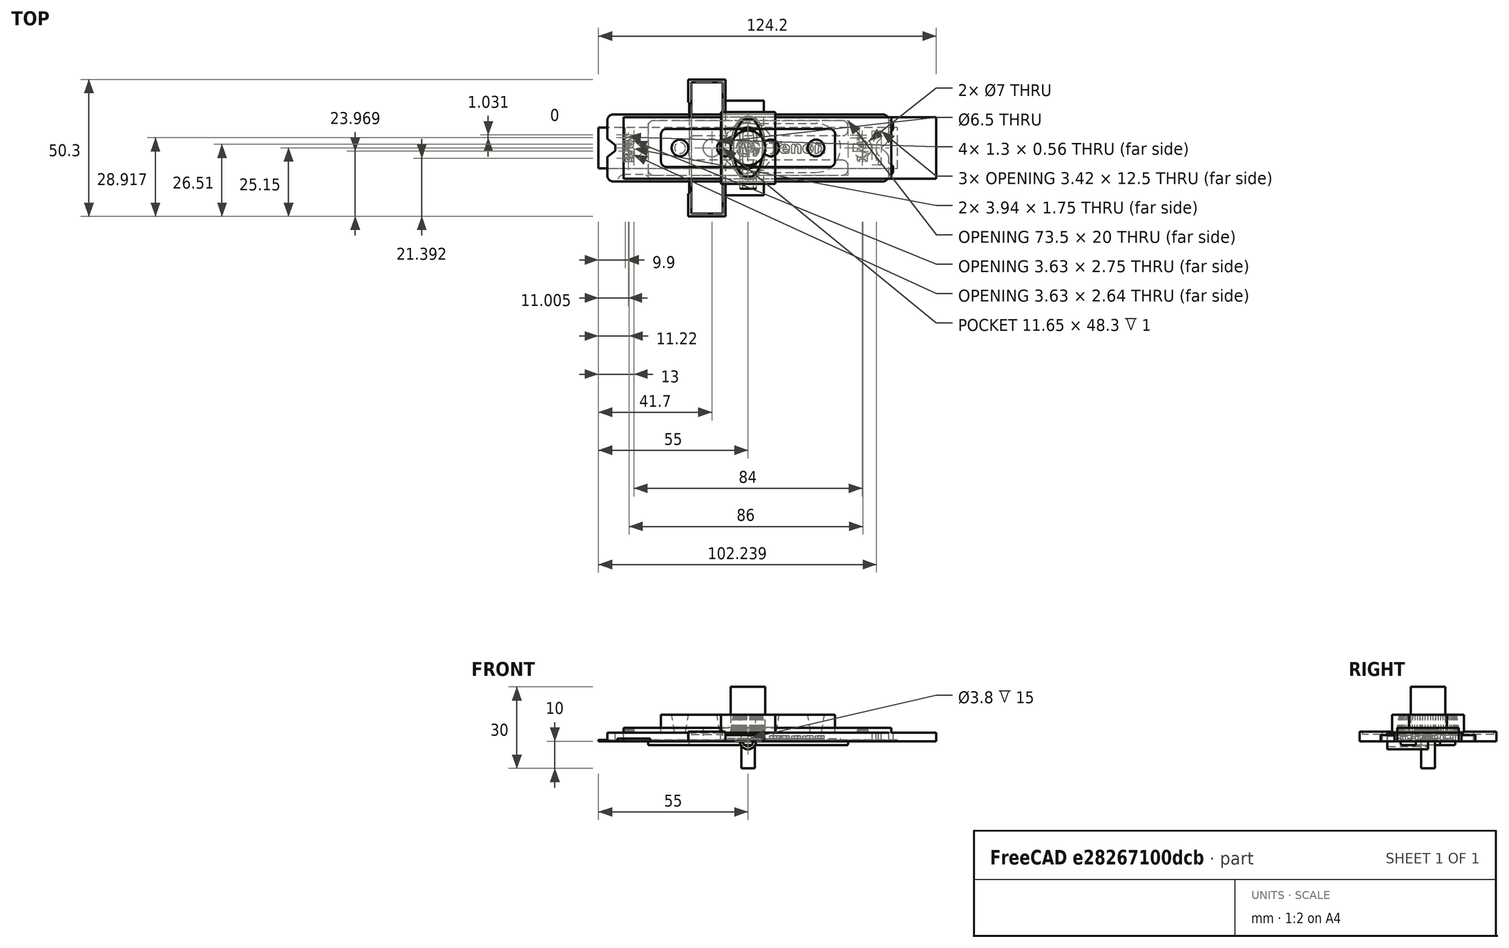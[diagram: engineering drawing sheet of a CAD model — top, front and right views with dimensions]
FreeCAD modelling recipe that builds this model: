
FCSTD DOCUMENT  (FreeCAD 1.1R20260325 (Git shallow))
Label: FMT Guide
License: All rights reserved
LicenseURL: http://en.wikipedia.org/wiki/All_rights_reserved
objects: Sketcher::SketchObject×25, PartDesign::Pad×16, App::Point×10, PartDesign::Body×10, PartDesign::Pocket×5, Part::Part2DObjectPython×4, Part::Extrusion×4, Part::Fuse×3, Part::MultiFuse×3, PartDesign::Plane×2, Part::Cut×2, Mesh::Feature×2, Spreadsheet::Sheet×1, Part::DatumPlane×1, PartDesign::Fillet×1, Part::Scale×1, Part::Loft×1, PartDesign::LinearPattern×1
note: 148 computed .brp shape members not serialized (recipe doc carries the construction recipe); baked Part::Feature solids carry a one-line shape summary decoded from their .brp

FEATURE [Sketcher::SketchObject] Sketch  label="Base Outline"
  ArcFitTolerance = 1e-06
  AttachmentSupport = -> [XY_Plane]
  ExternalTypes = [0]
  FullyConstrained = true
  MakeInternals = false
  MapMode = 5
  _ExternalGeoVersion = 0
  expr: Constraints[12] = Spreadsheet.Base_Corner_Radious
  expr: Constraints[18] = Spreadsheet.Base_Width
  expr: Constraints[19] = Spreadsheet.Base_Length
  sketch-geometry (32):
    g0: LineSegment StartX=-49.55 StartY=-12.32 StartZ=0 EndX=49.55 EndY=-12.32 EndZ=0
    g1: LineSegment [constr] StartX=51.75 StartY=-10.12 StartZ=0 EndX=51.75 EndY=10.12 EndZ=0
    g2: LineSegment StartX=49.55 StartY=12.32 StartZ=0 EndX=-49.55 EndY=12.32 EndZ=0
    g3: ArcOfCircle CenterX=-49.55 CenterY=10.12 CenterZ=0 NormalX=0 NormalY=0 NormalZ=1 AngleXU=0 Radius=2.2 StartAngle=1.5708 EndAngle=3.14159
    g4: ArcOfCircle CenterX=-49.55 CenterY=-10.12 CenterZ=0 NormalX=0 NormalY=0 NormalZ=1 AngleXU=0 Radius=2.2 StartAngle=3.14159 EndAngle=4.71239
    g5: ArcOfCircle CenterX=49.55 CenterY=-10.12 CenterZ=0 NormalX=0 NormalY=0 NormalZ=1 AngleXU=0 Radius=2.2 StartAngle=4.71239 EndAngle=6.28319
    g6: ArcOfCircle CenterX=49.55 CenterY=10.12 CenterZ=0 NormalX=0 NormalY=0 NormalZ=1 AngleXU=0 Radius=2.2 StartAngle=4e-16 EndAngle=1.5708
    g7: GeomPoint [constr] X=51.75 Y=-12.32 Z=0
    g8: LineSegment StartX=51.75 StartY=10.12 StartZ=0 EndX=51.75 EndY=3.625 EndZ=0
    g9: LineSegment StartX=51.75 StartY=-10.12 StartZ=0 EndX=51.75 EndY=-3.625 EndZ=0
    g10: ArcOfCircle CenterX=-49.55 CenterY=3.61127 CenterZ=0 NormalX=0 NormalY=0 NormalZ=1 AngleXU=0 Radius=2.2 StartAngle=3.14159 EndAngle=3.92699
    g11: ArcOfCircle CenterX=-49.55 CenterY=-3.61127 CenterZ=0 NormalX=0 NormalY=0 NormalZ=1 AngleXU=0 Radius=2.2 StartAngle=2.35619 EndAngle=3.14159
    g12: LineSegment StartX=51.5641 StartY=3.23597 StartZ=0 EndX=48.9359 EndY=1.11403 EndZ=0
    g13: LineSegment StartX=48.75 StartY=0.725 StartZ=0 EndX=48.75 EndY=-0.725 EndZ=0
    g14: LineSegment StartX=48.9359 StartY=-1.11403 StartZ=0 EndX=51.5641 EndY=-3.23597 EndZ=0
    g15: ArcOfCircle CenterX=51.25 CenterY=3.625 CenterZ=0 NormalX=0 NormalY=0 NormalZ=1 AngleXU=0 Radius=0.5 StartAngle=5.39161 EndAngle=6.28319
    g16: ArcOfCircle CenterX=51.25 CenterY=-3.625 CenterZ=0 NormalX=0 NormalY=0 NormalZ=1 AngleXU=0 Radius=0.5 StartAngle=6.28319 EndAngle=7.17476
    g17: ArcOfCircle CenterX=49.25 CenterY=-0.725 CenterZ=0 NormalX=0 NormalY=0 NormalZ=1 AngleXU=0 Radius=0.5 StartAngle=3.14159 EndAngle=4.03317
    g18: ArcOfCircle CenterX=49.25 CenterY=0.725 CenterZ=0 NormalX=0 NormalY=0 NormalZ=1 AngleXU=0 Radius=0.5 StartAngle=2.25002 EndAngle=3.14159
    g19: LineSegment StartX=-51.1056 StartY=2.05563 StartZ=0 EndX=-49.05 EndY=0 EndZ=0
    g20: LineSegment StartX=-49.05 StartY=0 StartZ=0 EndX=-51.1056 EndY=-2.05563 EndZ=0
    g21: LineSegment StartX=-48.95 StartY=5.75 StartZ=0 EndX=-48.95 EndY=3.5 EndZ=0
    g22: LineSegment StartX=-47.95 StartY=5.75 StartZ=0 EndX=-47.95 EndY=4.6 EndZ=0
    g23: ArcOfCircle CenterX=-48.45 CenterY=5.75 CenterZ=0 NormalX=0 NormalY=0 NormalZ=1 AngleXU=0 Radius=0.5 StartAngle=1e-16 EndAngle=3.14159
    g24: LineSegment StartX=-48.95 StartY=-3.5 StartZ=0 EndX=-48.95 EndY=-5.75 EndZ=0
    g25: LineSegment StartX=-47.95 StartY=-4.6 StartZ=0 EndX=-47.95 EndY=-5.75 EndZ=0
    g26: ArcOfCircle CenterX=-48.45 CenterY=-5.75 CenterZ=0 NormalX=0 NormalY=0 NormalZ=1 AngleXU=0 Radius=0.5 StartAngle=3.14159 EndAngle=6.28319
    g27: ArcOfCircle CenterX=-51.1056 CenterY=0 CenterZ=0 NormalX=0 NormalY=0 NormalZ=1 AngleXU=0 Radius=4.11057 StartAngle=5.26441 EndAngle=7.30196
    g28: ArcOfCircle CenterX=-51.1056 CenterY=0 CenterZ=0 NormalX=0 NormalY=0 NormalZ=1 AngleXU=0 Radius=5.57835 StartAngle=5.31366 EndAngle=7.25271
    g29: LineSegment StartX=-51.75 StartY=10.12 StartZ=0 EndX=-51.75 EndY=3.61127 EndZ=0
    g30: LineSegment StartX=-51.75 StartY=-3.61127 StartZ=0 EndX=-51.75 EndY=-10.12 EndZ=0
    g31: GeomPoint X=50.25 Y=2.175 Z=0
  constraints (79):
    c: Tangent(g0,g4) = -1.5708
    c: Tangent(g0,g5) = -1.5708
    c: Tangent(g1,g5) = -1.5708
    c: Tangent(g1,g6) = -1.5708
    c: Tangent(g2,g6) = -1.5708
    c: Tangent(g2,g3) = -1.5708
    c: Vertical(g1)
    c: Horizontal(g0)
    c: Horizontal(g2)
    c: Equal(g4,g5)
    c: PointOnObject(g7,g0)
    c: PointOnObject(g7,g1)
    c: Radius(g6) = 2.2
    c: Symmetric(g3,g6,g-2)
    c: Symmetric(g3,g4,g-1)
    c: Tangent(g6,g8)
    c: Coincident(g9,g1)
    c: Coincident(g8,g1)
    c: DistanceY(g0,g2) = 24.64
    c: DistanceX(g3,g1) = 103.5
    c: Equal(g3,g10)
    c: Tangent(g8,g15) = 1.5708
    c: Tangent(g12,g15) = 1.5708
    c: Tangent(g9,g16) = -1.5708
    c: Tangent(g14,g16) = 1.5708
    c: Tangent(g13,g17) = -1.5708
    c: Tangent(g14,g17) = -1.5708
    c: Tangent(g12,g18) = -1.5708
    c: Tangent(g13,g18) = -1.5708
    c: Equal(g15,g18)
    c: Equal(g18,g17)
    c: Equal(g17,g16)
    c: Radius(g15) = 0.5
    c: Symmetric(g18,g17,g-1)
    c: Symmetric(g15,g16,g-1)
    c: DistanceY(g16,g15) = 7.25
    c: DistanceY(g17,g18) = 1.45
    c: DistanceX(g18,g15) = 2
    c: Equal(g5,g6)
    c: PointOnObject(g19,g-1)
    c: Coincident(g20,g19)
    c: Angle(g19,g20) = 1.5708
    c: Tangent(g19,g10) = -1.5708
    c: Tangent(g20,g11) = -1.5708
    c: Symmetric(g10,g11,g-1)
    c: DistanceX(g10,g19) = 2.7
    c: Vertical(g21)
    c: Vertical(g22)
    c: Tangent(g23,g21) = -1.5708
    c: Tangent(g23,g22) = 1.5708
    c: Vertical(g22,g25)
    c: Vertical(g21,g24)
    c: Radius(g23) = 0.5
    c: Vertical(g24)
    c: Vertical(g25)
    c: Coincident(g26,g24)
    c: Coincident(g26,g25)
    c: Equal(g26,g23)
    c: Symmetric(g26,g23,g-1)
    c: Coincident(g27,g21)
    c: Coincident(g24,g27)
    c: PointOnObject(g27,g-1)
    c: Coincident(g28,g22)
    c: Coincident(g28,g25)
    c: Coincident(g27,g28)
    c: DistanceY(g26,g23) = 11.5
    c: DistanceX(g10,g23) = 3.3
    c: DistanceY(g21,g22) = 1.1
    c: DistanceY(g24,g21) = 7
    c: Vertical(g10,g27)
    c: Vertical(g30)
    c: Vertical(g29)
    c: Tangent(g10,g29) = -1.5708
    c: Tangent(g30,g11) = -1.5708
    c: Tangent(g3,g29) = -1.5708
    c: Tangent(g30,g4) = -1.5708
    c: DistanceY(g18,g15) = 2.9
    c: DistanceX(g19,g13) = 97.8
    c: Symmetric(g12,g12,g31)
FEATURE [Spreadsheet::Sheet] Spreadsheet
  cells = A1='Base; A2='Upper Title; B2(Upper_Title)='3/8"; A3='Lower Title; B3(Lower_Title)='1/4"; A4='Base Width; B4(Base_Width)=24.64; C4='Width of base of guide; A5='Base Length; B5(Base_Length)=103.5; C5='Length of base of guide; A6='Base Thickness; B6(Base_Thickness)=3.1; C6='Thickness of base of guide; A7='Base Corner Radious; B7(Base_Corner_Radious)=2.2; C7='Radii of base curves; A9='Lower Plane; B9(Lower_Plane)==Base_Thickness + 0.1; C9='Lower plane of guide portion; A10='Upper Plane; B10(Upper_Plane)==Lower_Plane + 6.5; C10='Upper plane of guide portion; A12='Pin Bottom Width; B12(Pin_Bottom_Width)=4; C12='Diameter of narrow point of Pin; A13='Pin Top Width; B13(Pin_Top_Width)=5; C13='Diameter of wide point of pin; A14='Pin Angle; B14(Pin_Angle)=9.22; A15='Calculated Pin Angle; B15==atan((Pin_Top_Width - Pin_Bottom_Width) / 3) / 2; A16='Bump Thickness; B16(Bump_Thickness)==Base_Thickness - 0.5; A17='Bump Width; B17(Bump_Width)=3.2; A18='Bump Spacing; B18(Bump_Spacing)=15.7; A19='Margin; B19(Margin)=1; A20='Pin Spacing; B20(Pin_Spacing)=250; A22='Mortise & Tenon; A23='Movement Ratio; B23(Movement_Ratio)=2; C23='Y-scale for guide; A24='Width; B24(Width)=6.35; C24='Width of tenon/mortise; A25='Length; B25(Length)=9.525; C25='Length of tenon/mortise; A26='Router Diameter; B26(Router_Diameter)==Width; C26='Always equals width of tenon; A27='Fix; B27(Fix)=0; C27='Hack for -ve dimension; A28='Width Delta; B28(Width_Delta)=1.75; C28='Extra Tenon Width; A29='Length Delta; B29(Length_Delta)=1; C29='Extra Tenon Length; A30='Slot Delta; B30(Slot_Delta)=1.35; C30='Extra Mortise Length; A32='Dowel Centres; A33='Dowel Extent; B33(Dowel_Extent)=50; C33='Extent of Dowels; A34='Dowel Length; B34(Dowel_Length)==Dowel_Extent + 10; C34='Length of base (calculated); A35='Dowel Width; B35(Dowel_Width)=10; C35='Width of base; A36='Dowel Number; B36(Dowel_Number)=4; A38='Centering Disk; A39='Centering Title; B39(Centering_Title)='1/2"; A40='Centering Disk Diameter; B40(Centering_Disk_Diameter)=18.8; A41='Centering Disk Thickness; B41(Centering_Disk_Thickness)=5; A42='Centering Post Diameter; B42(Centering_Post_Diameter)=12.7; A43='Centering Post Length; B43(Centering_Post_Length)=10; A45='Y Tenon; A46='Tenon Base Width; B46(Tenon_Base_Width)=20; A47='Tenon Extra Length; B47(Tenon_Extra_Length)=20
FEATURE [PartDesign::Plane] DatumPlane  label="Upper Plane"
  AttachmentOffset = pos=(0,0,9.7) rot=(0,0,1;0rad)
  AttachmentSupport = -> [XY_Plane]
  Length = 160.151
  MapMode = 5
  Placement = pos=(0,0,9.7) rot=(0,0,1;0rad)
  ResizeMode = 0
  Width = 133.592
  expr: .AttachmentOffset.Base.z = Spreadsheet.Upper_Plane
FEATURE [PartDesign::Plane] DatumPlane001  label="Mid Plane"
  AttachmentOffset = pos=(0,0,3.2) rot=(0,0,1;0rad)
  AttachmentSupport = -> [XY_Plane]
  Length = 160.151
  MapMode = 5
  Placement = pos=(0,0,3.2) rot=(0,0,1;0rad)
  ResizeMode = 0
  Width = 133.592
  expr: .AttachmentOffset.Base.z = Spreadsheet.Lower_Plane
FEATURE [Part::DatumPlane] DatumPlane002  label="Base Surface Plane"
  AttachmentSupport = -> [Origin]
  Placement = pos=(0,0,3.1) rot=(0,0,1;0rad)
  expr: .Placement.Base.z = Spreadsheet.Base_Thickness
FEATURE [PartDesign::Pad] Pad  label="Base Base"
  Direction = (0,0,1)
  Length = 3.1
  Length2 = 10
  Profile = -> Sketch
  ReferenceAxis = -> Sketch [N_Axis]
  SideType = 0
  Suppressed = false
  Type = 0
  Type2 = 0
  expr: Length = Spreadsheet.Base_Thickness
FEATURE [Part::Part2DObjectPython] ShapeString001  label="Label"  # Draft 2D object (typed FeaturePython)
  FontFile = <path>
  Fuse = false
  Justification = 4
  JustificationReference = 0
  KeepLeftMargin = false
  MakeFace = true
  ObliqueAngle = 0
  Placement = pos=(44,0,3.1) rot=(0,0,1;4.71239rad)
  ScaleToSize = true
  Size = 3.5
  String = 3/8"
  Tracking = 0
  expr: .Placement.Base.z = Spreadsheet.Base_Thickness
  expr: String = Spreadsheet.Upper_Title
FEATURE [Part::Extrusion] Extrude  label="Extrude Upper"
  Base = -> ShapeString001
  Dir = (0,0,1)
  DirMode = 2
  FaceMakerClass = Part::FaceMakerBullseye
  FaceMakerMode = 3
  InnerWireTaper = 0
  LengthFwd = 1
  LengthRev = 0
  Solid = false
  Symmetric = false
FEATURE [App::Point] Origin007  label="Origin008"
  Role = Origin
FEATURE [Sketcher::SketchObject] Sketch008
  ArcFitTolerance = 1e-06
  AttachmentSupport = -> [Origin006]
  ExternalTypes = [0]
  FullyConstrained = true
  MakeInternals = false
  MapMode = 5
  _ExternalGeoVersion = 1
  expr: Constraints[1] = Spreadsheet.Centering_Disk_Diameter
  sketch-geometry (1):
    g0: Circle CenterX=0 CenterY=0 CenterZ=0 NormalX=0 NormalY=0 NormalZ=1 AngleXU=0 Radius=9.4
  constraints (2):
    c: Coincident(g0,g-1)
    c: Diameter(g0) = 18.8
FEATURE [PartDesign::Pad] Pad002  label="Base001"
  Direction = (0,0,1)
  Length = 5
  Length2 = 10
  Profile = -> Sketch008
  ReferenceAxis = -> Sketch008 [N_Axis]
  SideType = 0
  Suppressed = false
  Type = 0
  Type2 = 0
  expr: Length = Spreadsheet.Centering_Disk_Thickness
FEATURE [Sketcher::SketchObject] Sketch009
  ArcFitTolerance = 1e-06
  AttachmentSupport = -> [Pad002]
  ExternalTypes = [0]
  FullyConstrained = true
  MakeInternals = false
  MapMode = 5
  Placement = pos=(0,0,5) rot=(0,0,1;0rad)
  _ExternalGeoVersion = 1
  expr: Constraints[1] = Spreadsheet.Centering_Post_Diameter
  sketch-geometry (1):
    g0: Circle CenterX=0 CenterY=0 CenterZ=0 NormalX=0 NormalY=0 NormalZ=1 AngleXU=0 Radius=6.35
  constraints (2):
    c: Coincident(g0,g-1)
    c: Diameter(g0) = 12.7
FEATURE [PartDesign::Pad] Pad003  label="Arbor"
  BaseFeature = -> Pad002
  Direction = (0,0,1)
  Length = 15
  Length2 = 10
  Profile = -> Sketch009
  ReferenceAxis = -> Sketch009 [N_Axis]
  SideType = 0
  Suppressed = false
  Type = 0
  Type2 = 0
  expr: Length = Spreadsheet.Centering_Post_Length + Spreadsheet.Centering_Disk_Thickness
FEATURE [PartDesign::Body] Body003  label="Centering Bare"
  AllowCompound = false
  Group = -> [Sketch008,Pad002,Sketch009,Pad003]
  Origin = -> Origin006
  Tip = -> Pad003
FEATURE [Sketcher::SketchObject] Sketch013  label="Outline"
  ArcFitTolerance = 1e-06
  AttachmentSupport = -> [DatumPlane002]
  ExternalTypes = [0]
  FullyConstrained = true
  MakeInternals = false
  MapMode = 5
  Placement = pos=(0,0,3.1) rot=(0,0,1;0rad)
  _ExternalGeoVersion = 1
  expr: Constraints[18] = Spreadsheet.Dowel_Length
  expr: Constraints[19] = Spreadsheet.Dowel_Width
  sketch-geometry (10):
    g0: LineSegment StartX=-32 StartY=5 StartZ=0 EndX=-32 EndY=-5 EndZ=0
    g1: LineSegment StartX=-30 StartY=-7 StartZ=0 EndX=30 EndY=-7 EndZ=0
    g2: LineSegment StartX=32 StartY=-5 StartZ=0 EndX=32 EndY=5 EndZ=0
    g3: LineSegment StartX=30 StartY=7 StartZ=0 EndX=-30 EndY=7 EndZ=0
    g4: ArcOfCircle CenterX=-30 CenterY=5 CenterZ=0 NormalX=0 NormalY=0 NormalZ=1 AngleXU=0 Radius=2 StartAngle=1.5708 EndAngle=3.14159
    g5: ArcOfCircle CenterX=-30 CenterY=-5 CenterZ=0 NormalX=0 NormalY=0 NormalZ=1 AngleXU=0 Radius=2 StartAngle=3.14159 EndAngle=4.71239
    g6: ArcOfCircle CenterX=30 CenterY=-5 CenterZ=0 NormalX=0 NormalY=0 NormalZ=1 AngleXU=0 Radius=2 StartAngle=4.71239 EndAngle=6.28319
    g7: ArcOfCircle CenterX=30 CenterY=5 CenterZ=0 NormalX=0 NormalY=0 NormalZ=1 AngleXU=0 Radius=2 StartAngle=0 EndAngle=1.5708
    g8: GeomPoint [constr] X=-32 Y=7 Z=0
    g9: GeomPoint [constr] X=32 Y=-7 Z=0
  constraints (22):
    c: Tangent(g0,g4) = -1.5708
    c: Tangent(g0,g5) = -1.5708
    c: Tangent(g1,g5) = -1.5708
    c: Tangent(g1,g6) = -1.5708
    c: Tangent(g2,g6) = -1.5708
    c: Tangent(g2,g7) = -1.5708
    c: Tangent(g3,g7) = -1.5708
    c: Tangent(g3,g4) = -1.5708
    c: Vertical(g0)
    c: Vertical(g2)
    c: Horizontal(g1)
    c: Horizontal(g3)
    c: Equal(g4,g5)
    c: PointOnObject(g8,g0)
    c: PointOnObject(g8,g3)
    c: PointOnObject(g9,g1)
    c: PointOnObject(g9,g2)
    c: Radius(g7) = 2
    c: DistanceX(g4,g7) = 60
    c: DistanceY(g6,g7) = 10
    c: Symmetric(g7,g6,g-1)
    c: Symmetric(g4,g7,g-2)
FEATURE [PartDesign::Pad] Pad004  label="Dowel Base"
  Direction = (0,0,1)
  Length = 6.6
  Length2 = 10
  Placement = pos=(0,0,3.1) rot=(0,0,1;0rad)
  Profile = -> Sketch013
  ReferenceAxis = -> Sketch013 [N_Axis]
  SideType = 0
  Suppressed = false
  Type = 0
  Type2 = 0
  expr: Length = Spreadsheet.Upper_Plane - Spreadsheet.Base_Thickness
FEATURE [App::Point] Origin009  label="Origin011"
  Role = Origin
FEATURE [App::Point] Origin002  label="Origin"
  Role = Origin
FEATURE [Part::Part2DObjectPython] ShapeString  # Draft 2D object (typed FeaturePython)
  FontFile = <path>
  Fuse = false
  Justification = 4
  JustificationReference = 0
  KeepLeftMargin = false
  MakeFace = true
  ObliqueAngle = 0
  Placement = pos=(0,0,0) rot=(1,0,0;3.14159rad)
  ScaleToSize = false
  Size = 3
  String = 1/2"
  Tracking = 0
  expr: String = Spreadsheet.Centering_Title
FEATURE [Part::Extrusion] Extrude001  label="Description"
  Base = -> ShapeString
  Dir = (0,0,-1)
  DirMode = 2
  FaceMakerClass = Part::FaceMakerBullseye
  FaceMakerMode = 3
  InnerWireTaper = 0
  LengthFwd = 1
  LengthRev = 0
  Reversed = true
  Solid = false
  Symmetric = false
FEATURE [Part::Part2DObjectPython] ShapeString002  # Draft 2D object (typed FeaturePython)
  FontFile = <path>
  Fuse = false
  Justification = 4
  JustificationReference = 0
  KeepLeftMargin = false
  MakeFace = true
  ObliqueAngle = 0
  Placement = pos=(-42,0,3.1) rot=(0,0,1;4.71239rad)
  ScaleToSize = true
  Size = 3.5
  String = 1/4"
  Tracking = 0
  expr: .Placement.Base.z = Spreadsheet.Base_Thickness
  expr: String = Spreadsheet.Lower_Title
FEATURE [Part::Extrusion] Extrude002  label="Extrude Lower"
  Base = -> ShapeString002
  Dir = (0,0,1)
  DirMode = 2
  FaceMakerClass = Part::FaceMakerBullseye
  FaceMakerMode = 3
  InnerWireTaper = 0
  LengthFwd = 1
  LengthRev = 0
  Solid = false
  Symmetric = false
FEATURE [Part::Fuse] Fusion006  label="UpperLowerLabel"
  Base = -> Extrude
  Tool = -> Extrude002
FEATURE [Part::Cut] Cut002  label="Centering"
  Base = -> Body003
  Tool = -> Extrude001
FEATURE [App::Point] Origin011  label="Origin013"
  Role = Origin
FEATURE [Sketcher::SketchObject] Sketch014  label="Tenon Surround Outline"
  ArcFitTolerance = 1e-06
  AttachmentSupport = -> [DatumPlane002]
  ExternalTypes = [0]
  FullyConstrained = true
  MakeInternals = false
  MapMode = 5
  Placement = pos=(0,0,3.1) rot=(0,0,1;0rad)
  _ExternalGeoVersion = 1
  expr: Constraints[10] = (Spreadsheet.Length - Spreadsheet.Width) * 2 + Spreadsheet.Tenon_Extra_Length
  expr: Constraints[11] = Spreadsheet.Tenon_Base_Width
  sketch-geometry (5):
    g0: LineSegment StartX=-10 StartY=13.175 StartZ=0 EndX=-10 EndY=-13.175 EndZ=0
    g1: LineSegment StartX=-10 StartY=-13.175 StartZ=0 EndX=10 EndY=-13.175 EndZ=0
    g2: LineSegment StartX=10 StartY=-13.175 StartZ=0 EndX=10 EndY=13.175 EndZ=0
    g3: LineSegment StartX=10 StartY=13.175 StartZ=0 EndX=-10 EndY=13.175 EndZ=0
    g4: GeomPoint [constr] X=0 Y=0 Z=0
  constraints (12):
    c: Coincident(g0,g1)
    c: Coincident(g1,g2)
    c: Coincident(g2,g3)
    c: Coincident(g3,g0)
    c: Vertical(g0)
    c: Vertical(g2)
    c: Horizontal(g1)
    c: Horizontal(g3)
    c: Symmetric(g2,g0,g4)
    c: Coincident(g4,g-1)
    c: DistanceY(g2,g2) = 26.35
    c: Distance(g3,g3) = 20
FEATURE [PartDesign::Pad] Pad005  label="X Tenon Surround"
  Direction = (0,0,1)
  Length = 6.6
  Length2 = 10
  Placement = pos=(0,0,3.1) rot=(0,0,1;0rad)
  Profile = -> Sketch014
  ReferenceAxis = -> Sketch014 [N_Axis]
  SideType = 0
  Suppressed = false
  Type = 0
  Type2 = 0
  expr: Length = Spreadsheet.Upper_Plane - Spreadsheet.Base_Thickness
FEATURE [Sketcher::SketchObject] Sketch016  label="Y Tenon Outline"
  ArcFitTolerance = 1e-06
  AttachmentSupport = -> [DatumPlane002]
  ExternalTypes = [0]
  FullyConstrained = true
  MakeInternals = false
  MapMode = 5
  Placement = pos=(0,0,3.1) rot=(0,0,1;0rad)
  _ExternalGeoVersion = 1
  expr: Constraints[0] = Spreadsheet.Pin_Bottom_Width / 2
  expr: Constraints[24] = Spreadsheet.Length - Spreadsheet.Router_Diameter + Spreadsheet.Slot_Delta
  expr: Constraints[25] = Spreadsheet.Pin_Spacing / 2
  expr: Constraints[7] = Spreadsheet.Router_Diameter
  sketch-geometry (24):
    g0: ArcOfCircle CenterX=0.0204773 CenterY=4.525 CenterZ=0 NormalX=0 NormalY=0 NormalZ=1 AngleXU=0 Radius=2 StartAngle=6.27413 EndAngle=9.41573
    g1: ArcOfCircle CenterX=0.0204773 CenterY=-4.525 CenterZ=0 NormalX=0 NormalY=0 NormalZ=1 AngleXU=0 Radius=2 StartAngle=3.15064 EndAngle=6.29224
    g2: GeomPoint [constr] X=125 Y=0 Z=0
    g3: ArcOfCircle [constr] CenterX=125 CenterY=2.2625 CenterZ=0 NormalX=0 NormalY=0 NormalZ=1 AngleXU=0 Radius=3.175 StartAngle=1e-16 EndAngle=3.14159
    g4: ArcOfCircle [constr] CenterX=125 CenterY=-2.2625 CenterZ=0 NormalX=0 NormalY=0 NormalZ=1 AngleXU=0 Radius=3.175 StartAngle=3.14159 EndAngle=6.28319
    g5: LineSegment [constr] StartX=128.175 StartY=2.2625 StartZ=0 EndX=128.175 EndY=-2.2625 EndZ=0
    g6: LineSegment [constr] StartX=121.825 StartY=2.2625 StartZ=0 EndX=121.825 EndY=-2.2625 EndZ=0
    g7: Circle [constr] CenterX=125 CenterY=2.2625 CenterZ=0 NormalX=0 NormalY=0 NormalZ=1 AngleXU=0 Radius=3.175
    g8: GeomPoint [constr] X=249.98 Y=0 Z=0
    g9: LineSegment [constr] StartX=0.0204773 StartY=4.525 StartZ=0 EndX=125 EndY=2.2625 EndZ=0
    g10: LineSegment [constr] StartX=125 StartY=2.2625 StartZ=0 EndX=249.98 EndY=0 EndZ=0
    g11: LineSegment [constr] StartX=0 StartY=0 StartZ=0 EndX=125 EndY=0 EndZ=0
    g12: LineSegment [constr] StartX=125 StartY=0 StartZ=0 EndX=250 EndY=0 EndZ=0
    g13: LineSegment [constr] StartX=-1.97944 StartY=4.5431 StartZ=0 EndX=2.0204 EndY=4.5069 EndZ=0
    g14: LineSegment [constr] StartX=-1.97944 StartY=-4.5431 StartZ=0 EndX=2.0204 EndY=-4.5069 EndZ=0
    g15: Circle [constr] CenterX=0 CenterY=0 CenterZ=0 NormalX=0 NormalY=0 NormalZ=1 AngleXU=0 Radius=2
    g16: ArcOfCircle CenterX=499.969 CenterY=4.93e-14 CenterZ=0 NormalX=0 NormalY=0 NormalZ=1 AngleXU=0 Radius=497.969 StartAngle=3.13254 EndAngle=3.15064
    g17: GeomPoint [constr] X=2 Y=0 Z=0
    g18: ArcOfCircle CenterX=499.969 CenterY=-6.03e-14 CenterZ=0 NormalX=0 NormalY=0 NormalZ=1 AngleXU=0 Radius=501.969 StartAngle=3.13254 EndAngle=3.15064
    g19: GeomPoint [constr] X=-2 Y=0 Z=0
    g20: GeomPoint [constr] X=125 Y=5.4375 Z=0
    g21: GeomPoint [constr] X=125 Y=-5.4375 Z=0
    g22: GeomPoint [constr] X=0 Y=6.5249 Z=0
    g23: GeomPoint [constr] X=0 Y=-6.5249 Z=0
  constraints (58):
    c: Radius(g0) = 2
    c: PointOnObject(g2,g-1)
    c: Tangent(g3,g5) = 1.5708
    c: Tangent(g3,g6) = -1.5708
    c: Tangent(g4,g5) = 1.5708
    c: Tangent(g4,g6) = -1.5708
    c: Equal(g3,g4)
    c: Diameter(g3) = 6.35
    c: Symmetric(g3,g4,g-1)
    c: Vertical(g3,g2)
    c: Equal(g7,g3)
    c: DistanceY(g1,g0) = 9.05
    c: PointOnObject(g8,g-1)
    c: Coincident(g9,g0)
    c: Coincident(g9,g7)
    c: Coincident(g10,g7)
    c: Coincident(g10,g8)
    c: Parallel(g10,g9)
    c: Coincident(g11,g2)
    c: Coincident(g12,g2)
    c: PointOnObject(g12,g-1)
    c: Equal(g12,g11)
    c: Equal(g11,g10)
    c: Equal(g10,g9)
    c: Distance(g3,g4) = 4.525
    c: Distance(g11) = 125
    c: Coincident(g11,g-1)
    c: Symmetric(g0,g1,g-1)
    c: Coincident(g13,g0)
    c: Coincident(g13,g0)
    c: PointOnObject(g0,g13)
    c: Symmetric(g0,g1,g-1)
    c: Coincident(g14,g1)
    c: Coincident(g14,g1)
    c: PointOnObject(g1,g14)
    c: Coincident(g15,g11)
    c: Equal(g15,g1)
    c: Coincident(g16,g1)
    c: Tangent(g16,g15)
    c: PointOnObject(g17,g16)
    c: PointOnObject(g17,g-1)
    c: Tangent(g16,g0) = 1.5708
    c: Coincident(g18,g0)
    c: Coincident(g18,g1)
    c: PointOnObject(g19,g18)
    c: PointOnObject(g19,g-1)
    c: Tangent(g18,g15)
    c: PointOnObject(g20,g3)
    c: PointOnObject(g21,g4)
    c: Vertical(g21,g4)
    c: Vertical(g4,g20)
    c: DistanceY(g21,g20) = 10.875
    c: Coincident(g7,g3)
    c: PointOnObject(g22,g0)
    c: PointOnObject(g23,g1)
    c: PointOnObject(g23,g-2)
    c: PointOnObject(g22,g-2)
    c: Distance(g22,g23) = 13.0498
FEATURE [Sketcher::SketchObject] Sketch019  label="Reinforcing Outline"
  ArcFitTolerance = 1e-06
  ExternalTypes = [0]
  FullyConstrained = true
  MakeInternals = false
  MapMode = 5
  Placement = pos=(0,0,0) rot=(1,0,0;3.14159rad)
  _ExternalGeoVersion = 1
  expr: Constraints[9] = Spreadsheet.Base_Length - 2 * 15
  sketch-geometry (24):
    g0: LineSegment StartX=-34.75 StartY=10 StartZ=0 EndX=34.75 EndY=10 EndZ=0
    g1: LineSegment StartX=36.75 StartY=8 StartZ=0 EndX=36.75 EndY=-8 EndZ=0
    g2: LineSegment StartX=34.75 StartY=-10 StartZ=0 EndX=-34.75 EndY=-10 EndZ=0
    g3: LineSegment StartX=-36.75 StartY=-8 StartZ=0 EndX=-36.75 EndY=-6.5 EndZ=0
    g4: LineSegment StartX=-34.75 StartY=-4.5 StartZ=0 EndX=19.75 EndY=-4.5 EndZ=0
    g5: LineSegment StartX=21.75 StartY=-2.5 StartZ=0 EndX=21.75 EndY=2.5 EndZ=0
    g6: LineSegment StartX=19.75 StartY=4.5 StartZ=0 EndX=-34.75 EndY=4.5 EndZ=0
    g7: LineSegment StartX=-36.75 StartY=6.5 StartZ=0 EndX=-36.75 EndY=8 EndZ=0
    g8: ArcOfCircle CenterX=34.75 CenterY=8 CenterZ=0 NormalX=0 NormalY=0 NormalZ=1 AngleXU=0 Radius=2 StartAngle=0 EndAngle=1.5708
    g9: GeomPoint [constr] X=36.75 Y=10 Z=0
    g10: ArcOfCircle CenterX=34.75 CenterY=-8 CenterZ=0 NormalX=0 NormalY=0 NormalZ=1 AngleXU=0 Radius=2 StartAngle=4.71239 EndAngle=6.28319
    g11: GeomPoint [constr] X=36.75 Y=-10 Z=0
    g12: ArcOfCircle CenterX=-34.75 CenterY=8 CenterZ=0 NormalX=0 NormalY=0 NormalZ=1 AngleXU=0 Radius=2 StartAngle=1.5708 EndAngle=3.14159
    g13: GeomPoint [constr] X=-36.75 Y=10 Z=0
    g14: ArcOfCircle CenterX=-34.75 CenterY=6.5 CenterZ=0 NormalX=0 NormalY=0 NormalZ=1 AngleXU=0 Radius=2 StartAngle=3.14159 EndAngle=4.71239
    g15: GeomPoint [constr] X=-36.75 Y=4.5 Z=0
    g16: ArcOfCircle CenterX=-34.75 CenterY=-6.5 CenterZ=0 NormalX=0 NormalY=0 NormalZ=1 AngleXU=0 Radius=2 StartAngle=1.5708 EndAngle=3.14159
    g17: GeomPoint [constr] X=-36.75 Y=-4.5 Z=0
    g18: ArcOfCircle CenterX=-34.75 CenterY=-8 CenterZ=0 NormalX=0 NormalY=0 NormalZ=1 AngleXU=0 Radius=2 StartAngle=3.14159 EndAngle=4.71239
    g19: GeomPoint [constr] X=-36.75 Y=-10 Z=0
    g20: ArcOfCircle CenterX=19.75 CenterY=2.5 CenterZ=0 NormalX=0 NormalY=0 NormalZ=1 AngleXU=0 Radius=2 StartAngle=2e-16 EndAngle=1.5708
    g21: GeomPoint [constr] X=21.75 Y=4.5 Z=0
    g22: ArcOfCircle CenterX=19.75 CenterY=-2.5 CenterZ=0 NormalX=0 NormalY=0 NormalZ=1 AngleXU=0 Radius=2 StartAngle=4.71239 EndAngle=6.28319
    g23: GeomPoint [constr] X=21.75 Y=-4.5 Z=0
  constraints (51):
    c: Horizontal(g4)
    c: Symmetric(g21,g23,g-1)
    c: Symmetric(g9,g11,g-1)
    c: Symmetric(g15,g17,g-1)
    c: Symmetric(g13,g19,g-1)
    c: Vertical(g7)
    c: Distance(g9,g11) = 20
    c: Distance(g23,g21) = 9
    c: Symmetric(g11,g19,g-2)
    c: DistanceX(g19,g11) = 73.5
    c: DistanceX(g23,g11) = 15
    c: PointOnObject(g9,g0)
    c: PointOnObject(g9,g1)
    c: Tangent(g0,g8) = 1.5708
    c: Tangent(g1,g8) = 1.5708
    c: PointOnObject(g11,g1)
    c: PointOnObject(g11,g2)
    c: Tangent(g1,g10) = 1.5708
    c: Tangent(g2,g10) = 1.5708
    c: PointOnObject(g13,g0)
    c: PointOnObject(g13,g7)
    c: Tangent(g0,g12) = 1.5708
    c: Tangent(g7,g12) = 1.5708
    c: PointOnObject(g15,g6)
    c: PointOnObject(g15,g7)
    c: Tangent(g6,g14) = 1.5708
    c: Tangent(g7,g14) = 1.5708
    c: PointOnObject(g17,g3)
    c: PointOnObject(g17,g4)
    c: Tangent(g3,g16) = 1.5708
    c: Tangent(g4,g16) = 1.5708
    c: PointOnObject(g19,g2)
    c: PointOnObject(g19,g3)
    c: Tangent(g2,g18) = 1.5708
    c: Tangent(g3,g18) = 1.5708
    c: PointOnObject(g21,g5)
    c: PointOnObject(g21,g6)
    c: Tangent(g5,g20) = -1.5708
    c: Tangent(g6,g20) = -1.5708
    c: PointOnObject(g23,g4)
    c: PointOnObject(g23,g5)
    c: Tangent(g4,g22) = -1.5708
    c: Tangent(g5,g22) = -1.5708
    c: Equal(g8,g12)
    c: Equal(g12,g14)
    c: Equal(g14,g16)
    c: Equal(g16,g18)
    c: Equal(g18,g20)
    c: Equal(g20,g22)
    c: Equal(g22,g10)
    c: Radius(g10) = 2
FEATURE [PartDesign::Pad] Pad007  label="Reinforcing"
  BaseFeature = -> Pad
  Direction = (0,-1e-16,-1)
  Length = 1.5
  Length2 = 10
  Profile = -> Sketch019
  ReferenceAxis = -> Sketch019 [N_Axis]
  SideType = 0
  Suppressed = false
  Type = 0
  Type2 = 0
FEATURE [PartDesign::Fillet] Fillet002  label="Reinforcing Fillet"
  Base = -> Pad007 [Face48]
  BaseFeature = -> Pad007
  Radius = 0.5
  SupportTransform = false
  Suppressed = false
  UseAllEdges = false
FEATURE [Sketcher::SketchObject] Sketch020
  ArcFitTolerance = 1e-06
  AttachmentSupport = -> [Fillet002]
  ExternalTypes = [0]
  FullyConstrained = true
  MakeInternals = false
  MapMode = 5
  Placement = pos=(0,0,0) rot=(1,0,0;3.14159rad)
  _ExternalGeoVersion = 1
  expr: Constraints[7] = -Spreadsheet.Base_Width / 2
  sketch-geometry (4):
    g0: ArcOfCircle CenterX=38.5 CenterY=-12.32 CenterZ=0 NormalX=0 NormalY=0 NormalZ=1 AngleXU=0 Radius=2.5 StartAngle=1.5708 EndAngle=4.71239
    g1: ArcOfCircle CenterX=45.5 CenterY=-12.32 CenterZ=0 NormalX=0 NormalY=0 NormalZ=1 AngleXU=0 Radius=2.5 StartAngle=4.71239 EndAngle=7.85398
    g2: LineSegment StartX=38.5 StartY=-9.82 StartZ=0 EndX=45.5 EndY=-9.82 EndZ=0
    g3: LineSegment StartX=38.5 StartY=-14.82 StartZ=0 EndX=45.5 EndY=-14.82 EndZ=0
  constraints (10):
    c: Tangent(g0,g2) = 1.5708
    c: Tangent(g0,g3) = -1.5708
    c: Tangent(g1,g2) = 1.5708
    c: Tangent(g1,g3) = -1.5708
    c: Equal(g0,g1)
    c: Horizontal(g2)
    c: Radius(g1) = 2.5
    c: DistanceY(g0) = -12.32
    c: DistanceX(g0,g1) = 7
    c: DistanceX(g0) = 38.5
FEATURE [PartDesign::Pocket] Pocket  label="Recess"
  BaseFeature = -> Fillet002
  Direction = (0,0,1)
  Length = 1
  Length2 = 5
  Profile = -> Sketch020
  ReferenceAxis = -> Sketch020 [N_Axis]
  SideType = 0
  Suppressed = false
  Type = 0
  Type2 = 0
FEATURE [Sketcher::SketchObject] Sketch005  label="Slot Outline"
  ArcFitTolerance = 1e-06
  AttacherType = Attacher::AttachEngine3D
  ExternalTypes = [0]
  FullyConstrained = false
  MakeInternals = false
  MapMode = 5
  Placement = pos=(0,0,3.1) rot=(0,0,1;0rad)
  _ExternalGeoVersion = 1
  expr: .Placement.Base.z = Spreadsheet.Base_Thickness
  expr: Constraints[24] = Spreadsheet.Length - Spreadsheet.Router_Diameter + Spreadsheet.Pin_Top_Width
  expr: Constraints[7] = Spreadsheet.Length - Spreadsheet.Router_Diameter + Spreadsheet.Slot_Delta
  expr: Constraints[8] = Spreadsheet.Pin_Bottom_Width / 2
  sketch-geometry (11):
    g0: ArcOfCircle CenterX=-2.2625 CenterY=0 CenterZ=0 NormalX=0 NormalY=0 NormalZ=1 AngleXU=0 Radius=2 StartAngle=1.5708 EndAngle=4.71239
    g1: ArcOfCircle CenterX=2.2625 CenterY=0 CenterZ=0 NormalX=0 NormalY=0 NormalZ=1 AngleXU=0 Radius=2 StartAngle=4.71239 EndAngle=7.85398
    g2: LineSegment StartX=-2.2625 StartY=2 StartZ=0 EndX=2.2625 EndY=2 EndZ=0
    g3: LineSegment StartX=-2.2625 StartY=-2 StartZ=0 EndX=2.2625 EndY=-2 EndZ=0
    g4: GeomPoint X=-4.2625 Y=0 Z=0
    g5: GeomPoint X=4.2625 Y=0 Z=0
    g6: LineSegment [constr] StartX=-4.0875 StartY=29.5438 StartZ=0 EndX=-4.0875 EndY=17.568 EndZ=0
    g7: LineSegment [constr] StartX=-4.0875 StartY=17.568 StartZ=0 EndX=4.0875 EndY=17.568 EndZ=0
    g8: LineSegment [constr] StartX=4.0875 StartY=17.568 StartZ=0 EndX=4.0875 EndY=29.5438 EndZ=0
    g9: LineSegment [constr] StartX=4.0875 StartY=29.5438 StartZ=0 EndX=-4.0875 EndY=29.5438 EndZ=0
    g10: GeomPoint [constr] X=0 Y=23.5559 Z=0
  constraints (25):
    c: Tangent(g0,g2) = 1.5708
    c: Tangent(g0,g3) = -1.5708
    c: Tangent(g1,g2) = 1.5708
    c: Tangent(g1,g3) = -1.5708
    c: Equal(g0,g1)
    c: PointOnObject(g0,g-1)
    c: Symmetric(g0,g1,g-2)
    c: Distance(g1,g0) = 4.525
    c: Radius(g1) = 2
    c: PointOnObject(g4,g0)
    c: PointOnObject(g5,g1)
    c: PointOnObject(g4,g-1)
    c: PointOnObject(g5,g-1)
    c: DistanceX(g4,g5) = 8.525
    c: Coincident(g6,g7)
    c: Coincident(g7,g8)
    c: Coincident(g8,g9)
    c: Coincident(g9,g6)
    c: Vertical(g6)
    c: Vertical(g8)
    c: Horizontal(g7)
    c: Horizontal(g9)
    c: Symmetric(g8,g6,g10)
    c: PointOnObject(g10,g-2)
    c: DistanceX(g9,g9) = 8.175
FEATURE [Part::Scale] Scale  label="Scaled Slot Outline"
  Base = -> Sketch005
  Placement = pos=(0,0,9.7) rot=(0,0,1;0rad)
  Uniform = false
  UniformScale = 1
  XScale = 1
  YScale = 1.5
  ZScale = 1
  expr: .Placement.Base.z = Spreadsheet.Upper_Plane
  expr: YScale = 6 / 4
FEATURE [Part::Loft] Loft  label="Slot (Loft)"
  Closed = false
  MaxDegree = 5
  Ruled = false
  Sections = -> [Sketch005,Scale]
  Solid = true
FEATURE [App::Point] Origin013  label="Origin016"
  Role = Origin
FEATURE [Sketcher::SketchObject] Sketch021
  ArcFitTolerance = 1e-06
  AttachmentSupport = -> [Origin012]
  ExternalTypes = [0]
  FullyConstrained = true
  MakeInternals = false
  MapMode = 5
  _ExternalGeoVersion = 1
  sketch-geometry (4):
    g0: ArcOfCircle CenterX=0 CenterY=0 CenterZ=0 NormalX=0 NormalY=0 NormalZ=1 AngleXU=0 Radius=9 StartAngle=1.5708 EndAngle=4.71239
    g1: ArcOfCircle CenterX=25 CenterY=0 CenterZ=0 NormalX=0 NormalY=0 NormalZ=1 AngleXU=0 Radius=9 StartAngle=4.71239 EndAngle=7.85398
    g2: LineSegment StartX=-4.34e-14 StartY=9 StartZ=0 EndX=25 EndY=9 EndZ=0
    g3: LineSegment StartX=6.3e-15 StartY=-9 StartZ=0 EndX=25 EndY=-9 EndZ=0
  constraints (9):
    c: Tangent(g0,g2) = 1.5708
    c: Tangent(g0,g3) = -1.5708
    c: Tangent(g1,g2) = 1.5708
    c: Tangent(g1,g3) = -1.5708
    c: Equal(g0,g1)
    c: PointOnObject(g1,g-1)
    c: Radius(g1) = 9
    c: Coincident(g0,g-1)
    c: DistanceX(g0,g1) = 25
FEATURE [PartDesign::Pad] Pad008
  Direction = (0,0,1)
  Length = 1
  Length2 = 10
  Profile = -> Sketch021
  ReferenceAxis = -> Sketch021 [N_Axis]
  SideType = 0
  Suppressed = false
  Type = 0
  Type2 = 0
FEATURE [Sketcher::SketchObject] Sketch022
  ArcFitTolerance = 1e-06
  AttachmentSupport = -> [Origin012]
  ExternalTypes = [0]
  FullyConstrained = true
  MakeInternals = false
  MapMode = 5
  _ExternalGeoVersion = 1
  sketch-geometry (1):
    g0: Circle CenterX=0 CenterY=0 CenterZ=0 NormalX=0 NormalY=0 NormalZ=1 AngleXU=0 Radius=2.5
  constraints (2):
    c: Coincident(g0,g-1)
    c: Diameter(g0) = 5
FEATURE [Sketcher::SketchObject] Sketch023
  ArcFitTolerance = 1e-06
  AttachmentSupport = -> [Origin012]
  ExternalTypes = [0]
  FullyConstrained = false
  MakeInternals = false
  MapMode = 5
  _ExternalGeoVersion = 1
  sketch-geometry (1):
    g0: Circle CenterX=0 CenterY=0 CenterZ=0 NormalX=0 NormalY=0 NormalZ=1 AngleXU=0 Radius=17.5985
  constraints (1):
    c: Coincident(g0,g-1)
FEATURE [Sketcher::SketchObject] Sketch024  label="Tenon Check"
  ArcFitTolerance = 1e-06
  ExternalTypes = [0]
  FullyConstrained = true
  MakeInternals = false
  _ExternalGeoVersion = 1
  sketch-geometry (13):
    g0: GeomPoint [constr] X=-50 Y=0 Z=0
    g1: GeomPoint [constr] X=50 Y=0 Z=0
    g2: ArcOfCircle [constr] CenterX=-10 CenterY=0 CenterZ=0 NormalX=0 NormalY=0 NormalZ=1 AngleXU=0 Radius=3 StartAngle=1.5708 EndAngle=4.71239
    g3: ArcOfCircle [constr] CenterX=10 CenterY=0 CenterZ=0 NormalX=0 NormalY=0 NormalZ=1 AngleXU=0 Radius=3 StartAngle=4.71239 EndAngle=7.85398
    g4: LineSegment [constr] StartX=-10 StartY=3 StartZ=0 EndX=10 EndY=3 EndZ=0
    g5: LineSegment [constr] StartX=-10 StartY=-3 StartZ=0 EndX=10 EndY=-3 EndZ=0
    g6: Circle [constr] CenterX=0 CenterY=6 CenterZ=0 NormalX=0 NormalY=0 NormalZ=1 AngleXU=0 Radius=3
    g7: ArcOfCircle CenterX=-60 CenterY=0 CenterZ=0 NormalX=0 NormalY=0 NormalZ=1 AngleXU=0 Radius=10 StartAngle=1.5708 EndAngle=4.71239
    g8: ArcOfCircle CenterX=-40 CenterY=0 CenterZ=0 NormalX=0 NormalY=0 NormalZ=1 AngleXU=0 Radius=10 StartAngle=4.71239 EndAngle=7.85398
    g9: LineSegment StartX=-60 StartY=10 StartZ=0 EndX=-40 EndY=10 EndZ=0
    g10: LineSegment StartX=-60 StartY=-10 StartZ=0 EndX=-40 EndY=-10 EndZ=0
    g11: Circle CenterX=-50 CenterY=12 CenterZ=0 NormalX=0 NormalY=0 NormalZ=1 AngleXU=0 Radius=2
    g12: LineSegment [constr] StartX=50 StartY=0 StartZ=0 EndX=-50 EndY=12 EndZ=0
  constraints (32):
    c: PointOnObject(g0,g-1)
    c: Symmetric(g0,g1,g-2)
    c: DistanceX(g0,g1) = 100
    c: Tangent(g2,g4) = 1.5708
    c: Tangent(g2,g5) = -1.5708
    c: Tangent(g3,g4) = 1.5708
    c: Tangent(g3,g5) = -1.5708
    c: Equal(g2,g3)
    c: PointOnObject(g2,g-1)
    c: Symmetric(g2,g3,g-2)
    c: Tangent(g6,g4)
    c: PointOnObject(g6,g-2)
    c: Tangent(g7,g9) = 1.5708
    c: Tangent(g7,g10) = -1.5708
    c: Tangent(g8,g9) = 1.5708
    c: Tangent(g8,g10) = -1.5708
    c: Equal(g7,g8)
    c: PointOnObject(g7,g-1)
    c: Equal(g10,g5)
    c: Symmetric(g7,g8,g0)
    c: DistanceX(g5,g5) = 20
    c: Diameter(g3) = 6
    c: Diameter(g11) = 4
    c: Tangent(g11,g9)
    c: Coincident(g12,g1)
    c: PointOnObject(g6,g12)
    c: Vertical(g12,g0)
    c: Coincident(g11,g12)
    c: DistanceY(g7,g7) = 20
    c: DistanceY(g7,g7) = 10
    c: Equal(g6,g3)
    c: DistanceY(g11) = 12
FEATURE [Part::Part2DObjectPython] ShapeString003  label="Tenon Text"  # Draft 2D object (typed FeaturePython)
  FontFile = <path>
  Fuse = false
  Justification = 6
  JustificationReference = 0
  KeepLeftMargin = false
  MakeFace = true
  ObliqueAngle = 0
  Placement = pos=(8,-2,1) rot=(0,0,1;0rad)
  ScaleToSize = true
  Size = 4.5
  String = Tenon
  Tracking = 0
FEATURE [Sketcher::SketchObject] Sketch025  label="Dowel Lower Outline"
  ArcFitTolerance = 1e-06
  AttachmentSupport = -> [DatumPlane002]
  ExternalTypes = [0]
  FullyConstrained = true
  MakeInternals = false
  MapMode = 5
  Placement = pos=(0,0,3.1) rot=(0,0,1;0rad)
  _ExternalGeoVersion = 1
  expr: Constraints[1] = Spreadsheet.Dowel_Extent / 2
  expr: Constraints[2] = Spreadsheet.Pin_Bottom_Width
  sketch-geometry (1):
    g0: Circle CenterX=-25 CenterY=0 CenterZ=0 NormalX=0 NormalY=0 NormalZ=1 AngleXU=0 Radius=2
  constraints (3):
    c: PointOnObject(g0,g-1)
    c: DistanceX(g0,g-1) = 25
    c: Diameter(g0) = 4
FEATURE [PartDesign::Pocket] Pocket001  label="Dowel Lower"
  BaseFeature = -> Pad004
  Direction = (0,0,-1)
  Length = 6.6
  Length2 = 5
  Placement = pos=(0,0,3.1) rot=(0,0,1;0rad)
  Profile = -> Sketch025
  ReferenceAxis = -> Sketch025 [N_Axis]
  Reversed = true
  SideType = 0
  Suppressed = false
  TaperAngle = 9.22
  Type = 0
  Type2 = 0
  expr: Length = Spreadsheet.Upper_Plane - Spreadsheet.Base_Thickness
  expr: TaperAngle = Spreadsheet.Pin_Angle
FEATURE [PartDesign::LinearPattern] LinearPattern
  BaseFeature = -> Pocket001
  Direction = -> Sketch025 [H_Axis]
  Direction2 = -> Sketch025 [V_Axis]
  Length = 50
  Length2 = 100
  Mode = 0
  Mode2 = 0
  Occurrences = 4
  Occurrences2 = 1
  Offset = 16.6667
  Offset2 = 100
  Originals = -> [Pocket001]
  Placement = pos=(0,0,3.1) rot=(0,0,1;0rad)
  Reversed2 = false
  SpacingPattern = [0]
  SpacingPattern2 = [0]
  Spacings = [-1,-1,-1]
  Suppressed = false
  TransformMode = 0
  expr: Length = Spreadsheet.Dowel_Extent
  expr: Occurrences = Spreadsheet.Dowel_Number
FEATURE [PartDesign::Body] Body004  label="Dowel Guide"
  AllowCompound = false
  Group = -> [Sketch013,Pad004,Sketch025,Pocket001,LinearPattern]
  Origin = -> Origin008
  Tip = -> LinearPattern
FEATURE [Part::Extrusion] Extrude004  label="Tenon Text Extrude"
  Base = -> ShapeString003
  Dir = (0,0,1)
  DirMode = 2
  FaceMakerClass = Part::FaceMakerBullseye
  FaceMakerMode = 3
  InnerWireTaper = 0
  LengthFwd = 1
  LengthRev = 0
  Solid = true
  Symmetric = false
FEATURE [PartDesign::Pocket] Pocket002  label="Y Tenon Template"
  BaseFeature = -> Pad005
  Direction = (0,0,-1)
  Length = 6.6
  Length2 = 5
  Placement = pos=(0,0,3.1) rot=(0,0,1;0rad)
  Profile = -> Sketch016
  ReferenceAxis = -> Sketch016 [N_Axis]
  Reversed = true
  SideType = 0
  Suppressed = false
  TaperAngle = 9.22
  Type = 0
  Type2 = 0
  expr: Length = Spreadsheet.Upper_Plane - Spreadsheet.Base_Thickness
  expr: TaperAngle = Spreadsheet.Pin_Angle
FEATURE [PartDesign::Body] Body005  label="Y Tenon Guide"
  AllowCompound = true
  Group = -> [Pad005,Sketch014,Sketch016,Pocket002]
  Origin = -> Origin010
  Tip = -> Pocket002
FEATURE [PartDesign::Pad] Pad010
  BaseFeature = -> Pad008
  Direction = (0,0,1)
  Length = 10
  Length2 = 10
  Profile = -> Sketch022
  ReferenceAxis = -> Sketch022 [N_Axis]
  Reversed = true
  SideType = 0
  Suppressed = false
  Type = 0
  Type2 = 0
FEATURE [PartDesign::Body] Body006  label="Router Depth Base"
  AllowCompound = false
  Group = -> [Sketch021,Pad008,Sketch022,Sketch023,Pad010]
  Origin = -> Origin012
  Tip = -> Pad010
FEATURE [Part::MultiFuse] Fusion010  label="Tenon Depth Guide"
  Shapes = -> [Body006,Extrude004]
FEATURE [Sketcher::SketchObject] Sketch026  label="Bump Outline"
  ArcFitTolerance = 1e-06
  AttachmentSupport = -> [DatumPlane002]
  ExternalGeometry = -> [Sketch]
  ExternalTypes = [0,0]
  FullyConstrained = true
  MakeInternals = false
  MapMode = 5
  Placement = pos=(0,0,3.1) rot=(0,0,1;0rad)
  _ExternalGeoVersion = 1
  expr: Constraints[13] = Spreadsheet.Bump_Width / 2
  expr: Constraints[15] = -Spreadsheet.Base_Length / 2
  sketch-geometry (9):
    g0: ArcOfCircle CenterX=-51.75 CenterY=8.52 CenterZ=0 NormalX=0 NormalY=0 NormalZ=1 AngleXU=0 Radius=1.6 StartAngle=1e-16 EndAngle=3.14159
    g1: ArcOfCircle CenterX=-51.75 CenterY=7.35 CenterZ=0 NormalX=0 NormalY=0 NormalZ=1 AngleXU=0 Radius=1.6 StartAngle=3.14159 EndAngle=6.28319
    g2: LineSegment StartX=-50.15 StartY=8.52 StartZ=0 EndX=-50.15 EndY=7.35 EndZ=0
    g3: LineSegment StartX=-53.35 StartY=8.52 StartZ=0 EndX=-53.35 EndY=7.35 EndZ=0
    g4: ArcOfCircle CenterX=-51.75 CenterY=-7.35 CenterZ=0 NormalX=0 NormalY=0 NormalZ=1 AngleXU=0 Radius=1.6 StartAngle=0 EndAngle=3.14159
    g5: ArcOfCircle CenterX=-51.75 CenterY=-8.52 CenterZ=0 NormalX=0 NormalY=0 NormalZ=1 AngleXU=0 Radius=1.6 StartAngle=3.14159 EndAngle=6.28319
    g6: LineSegment StartX=-50.15 StartY=-7.35 StartZ=0 EndX=-50.15 EndY=-8.52 EndZ=0
    g7: LineSegment StartX=-53.35 StartY=-7.35 StartZ=0 EndX=-53.35 EndY=-8.52 EndZ=0
    g8: GeomPoint X=-51.75 Y=5.75 Z=0
  constraints (20):
    c: Tangent(g0,g2) = 1.5708
    c: Tangent(g0,g3) = -1.5708
    c: Tangent(g1,g2) = 1.5708
    c: Tangent(g1,g3) = -1.5708
    c: Equal(g0,g1)
    c: Vertical(g2)
    c: Tangent(g4,g6) = 1.5708
    c: Tangent(g4,g7) = -1.5708
    c: Tangent(g5,g6) = 1.5708
    c: Tangent(g5,g7) = -1.5708
    c: Equal(g4,g5)
    c: Symmetric(g1,g4,g-1)
    c: Equal(g4,g0)
    c: Radius(g0) = 1.6
    c: Symmetric(g0,g5,g-1)
    c: DistanceX(g1) = -51.75
    c: PointOnObject(g8,g1)
    c: Vertical(g8,g1)
    c: Horizontal(g8,g-3)
    c: PointOnObject(g-4,g0)
FEATURE [PartDesign::Pad] Pad011  label="Bump"
  BaseFeature = -> Pocket
  Direction = (0,0,1)
  Length = 2.6
  Length2 = 10
  Profile = -> Sketch026
  ReferenceAxis = -> Sketch026 [N_Axis]
  Reversed = true
  SideType = 0
  Suppressed = false
  Type = 0
  Type2 = 0
  expr: Length = Spreadsheet.Bump_Thickness
FEATURE [PartDesign::Body] Body  label="Base"
  AllowCompound = false
  Group = -> [Sketch,Pad,Sketch019,Pad007,Fillet002,Sketch020,Pocket,Sketch026,Pad011]
  Origin = -> Origin
  Tip = -> Pad011
FEATURE [Part::MultiFuse] Fusion007  label="Base with Text"
  Placement = pos=(0,0,0) rot=(0,0,1;3.14159rad)
  Shapes = -> [Fusion006,Body]
FEATURE [Part::MultiFuse] Fusion  label="Dowling Guides"
  Shapes = -> [Body004,Fusion007]
FEATURE [App::Point] Origin015  label="Origin019"
  Role = Origin
FEATURE [Sketcher::SketchObject] Sketch027
  ArcFitTolerance = 1e-06
  AttachmentSupport = -> [Origin014]
  ExternalTypes = [0]
  FullyConstrained = true
  MakeInternals = false
  MapMode = 5
  Placement = pos=(0,0,0) rot=(1,0,0;1.5708rad)
  _ExternalGeoVersion = 1
  sketch-geometry (2):
    g0: Circle CenterX=0 CenterY=0 CenterZ=0 NormalX=0 NormalY=0 NormalZ=1 AngleXU=0 Radius=1.9
    g1: Circle CenterX=0 CenterY=0 CenterZ=0 NormalX=0 NormalY=0 NormalZ=1 AngleXU=0 Radius=3
  constraints (4):
    c: Coincident(g0,g-1)
    c: Coincident(g1,g0)
    c: Diameter(g1) = 6
    c: Diameter(g0) = 3.8
FEATURE [PartDesign::Pad] Pad012
  Direction = (0,-1,0)
  Length = 15
  Length2 = 10
  Profile = -> Sketch027
  ReferenceAxis = -> Sketch027 [N_Axis]
  SideType = 0
  Suppressed = false
  Type = 0
  Type2 = 0
FEATURE [PartDesign::Body] Body007  label="Depth Gauge Cylinder"
  AllowCompound = false
  Group = -> [Sketch027,Pad012]
  Origin = -> Origin014
  Tip = -> Pad012
FEATURE [App::Point] Origin017  label="Origin022"
  Role = Origin
FEATURE [Sketcher::SketchObject] Sketch028  label="Tab Outline"
  ArcFitTolerance = 1e-06
  AttachmentSupport = -> [Origin016]
  ExternalTypes = [0]
  FullyConstrained = true
  MakeInternals = false
  MapMode = 5
  _ExternalGeoVersion = 1
  sketch-geometry (8):
    g0: LineSegment StartX=-9.2 StartY=-17.45 StartZ=0 EndX=5.8 EndY=-17.45 EndZ=0
    g1: LineSegment StartX=5.8 StartY=-17.45 StartZ=0 EndX=5.8 EndY=-8.225 EndZ=0
    g2: LineSegment StartX=5.8 StartY=-8.225 StartZ=0 EndX=0 EndY=-9.225 EndZ=0
    g3: LineSegment StartX=0 StartY=-9.225 StartZ=0 EndX=0 EndY=9.225 EndZ=0
    g4: LineSegment StartX=0 StartY=9.225 StartZ=0 EndX=5.8 EndY=8.225 EndZ=0
    g5: LineSegment StartX=5.8 StartY=8.225 StartZ=0 EndX=5.8 EndY=17.45 EndZ=0
    g6: LineSegment StartX=-9.2 StartY=17.45 StartZ=0 EndX=5.8 EndY=17.45 EndZ=0
    g7: LineSegment StartX=-9.2 StartY=17.45 StartZ=0 EndX=-9.2 EndY=-17.45 EndZ=0
  constraints (20):
    c: Coincident(g0,g1)
    c: Coincident(g1,g2)
    c: Coincident(g2,g3)
    c: Coincident(g3,g4)
    c: Coincident(g4,g5)
    c: Vertical(g5)
    c: Symmetric(g3,g2,g-1)
    c: Symmetric(g4,g1,g-1)
    c: Horizontal(g0)
    c: Coincident(g6,g5)
    c: Symmetric(g5,g0,g-1)
    c: Symmetric(g6,g0,g-1)
    c: DistanceY(g0,g5) = 34.9
    c: DistanceY(g1,g4) = 16.45
    c: PointOnObject(g-1,g3)
    c: DistanceY(g3,g3) = 18.45
    c: Coincident(g7,g6)
    c: Coincident(g7,g0)
    c: DistanceX(g4) = 5.8
    c: DistanceX(g6,g6) = 15
FEATURE [PartDesign::Pad] Pad013
  Direction = (0,0,1)
  Length = 2.2
  Length2 = 10
  Profile = -> Sketch028
  ReferenceAxis = -> Sketch028 [N_Axis]
  SideType = 0
  Suppressed = false
  Type = 0
  Type2 = 0
FEATURE [Sketcher::SketchObject] Sketch030  label="Spacer Outline"
  ArcFitTolerance = 1e-06
  AttachmentSupport = -> [Origin016]
  ExternalTypes = [0]
  FullyConstrained = true
  MakeInternals = false
  MapMode = 5
  _ExternalGeoVersion = 1
  sketch-geometry (8):
    g0: LineSegment StartX=-22 StartY=25.15 StartZ=0 EndX=-22 EndY=16.75 EndZ=0
    g1: LineSegment StartX=-22 StartY=-25.15 StartZ=0 EndX=-8.25 EndY=-25.15 EndZ=0
    g2: LineSegment StartX=-8.25 StartY=-25.15 StartZ=0 EndX=-8.25 EndY=25.15 EndZ=0
    g3: LineSegment StartX=-22 StartY=25.15 StartZ=0 EndX=-8.25 EndY=25.15 EndZ=0
    g4: LineSegment StartX=-21.65 StartY=16.75 StartZ=0 EndX=-21.65 EndY=-16.75 EndZ=0
    g5: LineSegment StartX=-21.65 StartY=16.75 StartZ=0 EndX=-22 EndY=16.75 EndZ=0
    g6: LineSegment StartX=-21.65 StartY=-16.75 StartZ=0 EndX=-22 EndY=-16.75 EndZ=0
    g7: LineSegment StartX=-22 StartY=-16.75 StartZ=0 EndX=-22 EndY=-25.15 EndZ=0
  constraints (22):
    c: Coincident(g7,g1)
    c: Horizontal(g1)
    c: Coincident(g1,g2)
    c: Symmetric(g0,g7,g-1)
    c: Vertical(g2)
    c: Coincident(g3,g0)
    c: Horizontal(g3)
    c: DistanceY(g7,g0) = 50.3
    c: DistanceX(g3,g3) = 13.75
    c: DistanceX(g7,g-1) = 22
    c: Symmetric(g4,g4,g-1)
    c: DistanceY(g4,g4) = 33.5
    c: Coincident(g5,g4)
    c: Coincident(g6,g4)
    c: Horizontal(g6)
    c: Coincident(g5,g0)
    c: Coincident(g6,g7)
    c: Horizontal(g5)
    c: Distance(g5,g5) = 0.35
    c: Vertical(g0)
    c: Vertical(g7)
    c: Coincident(g2,g3)
FEATURE [PartDesign::Pad] Pad014
  BaseFeature = -> Pad013
  Direction = (0,0,1)
  Length = 3.5
  Length2 = 10
  Profile = -> Sketch030
  ReferenceAxis = -> Sketch030 [N_Axis]
  SideType = 0
  Suppressed = false
  Type = 0
  Type2 = 0
FEATURE [Sketcher::SketchObject] Sketch031
  ArcFitTolerance = 1e-06
  AttachmentSupport = -> [Pad014]
  ExternalGeometry = -> [Pad014]
  ExternalTypes = [0,0]
  FullyConstrained = true
  MakeInternals = false
  MapMode = 5
  Placement = pos=(0,0,3.5) rot=(0,0,1;0rad)
  _ExternalGeoVersion = 1
  sketch-geometry (4):
    g0: LineSegment StartX=-20.9 StartY=24.15 StartZ=0 EndX=-20.9 EndY=-24.15 EndZ=0
    g1: LineSegment StartX=-20.9 StartY=-24.15 StartZ=0 EndX=-9.25 EndY=-24.15 EndZ=0
    g2: LineSegment StartX=-9.25 StartY=-24.15 StartZ=0 EndX=-9.25 EndY=24.15 EndZ=0
    g3: LineSegment StartX=-9.25 StartY=24.15 StartZ=0 EndX=-20.9 EndY=24.15 EndZ=0
  constraints (11):
    c: Coincident(g0,g1)
    c: Coincident(g1,g2)
    c: Coincident(g2,g3)
    c: Coincident(g3,g0)
    c: Vertical(g0)
    c: Horizontal(g1)
    c: Horizontal(g3)
    c: Symmetric(g2,g1,g-1)
    c: DistanceY(g2,g-3) = 1
    c: DistanceX(g2,g-3) = 1
    c: DistanceX(g-4,g0) = 1.1
FEATURE [PartDesign::Pocket] Pocket003
  BaseFeature = -> Pad014
  Direction = (0,0,-1)
  Length = 1
  Length2 = 5
  Profile = -> Sketch031
  ReferenceAxis = -> Sketch031 [N_Axis]
  SideType = 0
  Suppressed = false
  Type = 0
  Type2 = 0
FEATURE [PartDesign::Body] Body008  label="Single Pass Dovetail Spacer"
  AllowCompound = false
  Group = -> [Sketch028,Pad013,Sketch030,Pad014,Sketch031,Pocket003]
  Origin = -> Origin016
  Tip = -> Pocket003
FEATURE [App::Point] Origin019  label="Origin024"
  Role = Origin
FEATURE [Sketcher::SketchObject] Sketch032
  ArcFitTolerance = 1e-06
  AttachmentSupport = -> [Origin018]
  ExternalTypes = [0]
  FullyConstrained = false
  MakeInternals = false
  MapMode = 5
  _ExternalGeoVersion = 1
  sketch-geometry (4):
    g0: LineSegment StartX=-45.8001 StartY=11.3 StartZ=0 EndX=-45.8001 EndY=-11.3 EndZ=0
    g1: LineSegment StartX=-45.8001 StartY=-11.3 StartZ=0 EndX=69.1999 EndY=-11.3 EndZ=0
    g2: LineSegment StartX=69.1999 StartY=-11.3 StartZ=0 EndX=69.1999 EndY=11.3 EndZ=0
    g3: LineSegment StartX=69.1999 StartY=11.3 StartZ=0 EndX=-45.8001 EndY=11.3 EndZ=0
  constraints (10):
    c: Coincident(g0,g1)
    c: Coincident(g1,g2)
    c: Coincident(g2,g3)
    c: Coincident(g3,g0)
    c: Vertical(g2)
    c: Horizontal(g1)
    c: Horizontal(g3)
    c: DistanceX(g3,g3) = 115
    c: DistanceY(g2,g2) = 22.6
    c: Symmetric(g0,g0,g-1)
FEATURE [PartDesign::Pad] Pad015
  Direction = (0,0,1)
  Length = 3.1
  Length2 = 10
  Profile = -> Sketch032
  ReferenceAxis = -> Sketch032 [N_Axis]
  SideType = 0
  Suppressed = false
  Type = 0
  Type2 = 0
FEATURE [Sketcher::SketchObject] Sketch033
  ArcFitTolerance = 1e-06
  AttachmentSupport = -> [Pad015]
  ExternalGeometry = -> [Pad015]
  ExternalTypes = [0,0]
  FullyConstrained = true
  MakeInternals = false
  MapMode = 5
  Placement = pos=(0,0,3.1) rot=(0,0,1;0rad)
  _ExternalGeoVersion = 1
  sketch-geometry (4):
    g0: LineSegment StartX=-45.8001 StartY=11.3 StartZ=0 EndX=-45.8001 EndY=-11.3 EndZ=0
    g1: LineSegment StartX=-45.8001 StartY=-11.3 StartZ=0 EndX=52.6999 EndY=-11.3 EndZ=0
    g2: LineSegment StartX=52.6999 StartY=-11.3 StartZ=0 EndX=52.6999 EndY=11.3 EndZ=0
    g3: LineSegment StartX=52.6999 StartY=11.3 StartZ=0 EndX=-45.8001 EndY=11.3 EndZ=0
  constraints (10):
    c: Coincident(g0,g1)
    c: Coincident(g1,g2)
    c: Coincident(g2,g3)
    c: Coincident(g3,g0)
    c: Vertical(g2)
    c: Horizontal(g1)
    c: Horizontal(g3)
    c: Coincident(g0,g-3)
    c: Coincident(g0,g-4)
    c: DistanceX(g3,g3) = 98.5
FEATURE [PartDesign::Pad] Pad016
  BaseFeature = -> Pad015
  Direction = (0,0,1)
  Length = 1.85
  Length2 = 10
  Profile = -> Sketch033
  ReferenceAxis = -> Sketch033 [N_Axis]
  SideType = 0
  Suppressed = false
  Type = 0
  Type2 = 0
FEATURE [Sketcher::SketchObject] Sketch034
  ArcFitTolerance = 1e-06
  AttachmentSupport = -> [Origin018]
  ExternalGeometry = -> [Sketch032]
  ExternalTypes = [0]
  FullyConstrained = true
  MakeInternals = false
  MapMode = 5
  _ExternalGeoVersion = 1
  sketch-geometry (1):
    g0: Circle CenterX=-13.3001 CenterY=0 CenterZ=0 NormalX=0 NormalY=0 NormalZ=1 AngleXU=0 Radius=3.25
  constraints (3):
    c: PointOnObject(g0,g-1)
    c: Diameter(g0) = 6.5
    c: DistanceX(g-3,g0) = 32.5
FEATURE [PartDesign::Pocket] Pocket004  label="Final"
  BaseFeature = -> Pad016
  Direction = (0,0,-1)
  Length = 5
  Length2 = 5
  Profile = -> Sketch034
  ReferenceAxis = -> Sketch034 [N_Axis]
  Reversed = true
  SideType = 0
  Suppressed = false
  Type = 1
  Type2 = 0
FEATURE [PartDesign::Body] Body009  label="Wrench"
  AllowCompound = false
  Group = -> [Sketch032,Pad015,Sketch033,Pad016,Sketch034,Pocket004]
  Origin = -> Origin018
  Tip = -> Pocket004
FEATURE [App::Point] Origin021  label="Origin027"
  Role = Origin
FEATURE [Sketcher::SketchObject] Sketch035
  ArcFitTolerance = 1e-06
  AttachmentSupport = -> [Origin020]
  ExternalTypes = [0]
  FullyConstrained = true
  MakeInternals = false
  MapMode = 5
  _ExternalGeoVersion = 1
  sketch-geometry (7):
    g0: LineSegment StartX=-55 StartY=7.5 StartZ=0 EndX=-55 EndY=-7.5 EndZ=0
    g1: LineSegment StartX=-55 StartY=-7.5 StartZ=0 EndX=55 EndY=-7.5 EndZ=0
    g2: LineSegment StartX=55 StartY=-7.5 StartZ=0 EndX=55 EndY=7.5 EndZ=0
    g3: LineSegment StartX=55 StartY=7.5 StartZ=0 EndX=-55 EndY=7.5 EndZ=0
    g4: GeomPoint [constr] X=0 Y=0 Z=0
    g5: Circle CenterX=-42 CenterY=0 CenterZ=0 NormalX=0 NormalY=0 NormalZ=1 AngleXU=0 Radius=3.5
    g6: Circle CenterX=42 CenterY=0 CenterZ=0 NormalX=0 NormalY=0 NormalZ=1 AngleXU=0 Radius=3.5
  constraints (17):
    c: Coincident(g0,g1)
    c: Coincident(g1,g2)
    c: Coincident(g2,g3)
    c: Coincident(g3,g0)
    c: Vertical(g0)
    c: Vertical(g2)
    c: Horizontal(g1)
    c: Horizontal(g3)
    c: Symmetric(g2,g0,g4)
    c: Coincident(g4,g-1)
    c: PointOnObject(g5,g-1)
    c: Symmetric(g5,g6,g-2)
    c: DistanceX(g5,g6) = 84
    c: DistanceX(g3,g3) = 110
    c: DistanceY(g2,g2) = 15
    c: Equal(g6,g5)
    c: Diameter(g6) = 7
FEATURE [PartDesign::Pad] Pad017
  Direction = (0,0,1)
  Length = 0.5
  Length2 = 10
  Profile = -> Sketch035
  ReferenceAxis = -> Sketch035 [N_Axis]
  SideType = 0
  Suppressed = false
  Type = 0
  Type2 = 0
FEATURE [PartDesign::Body] Body010  label="D4 Spacer"
  AllowCompound = false
  Group = -> [Sketch035,Pad017]
  Origin = -> Origin020
  Tip = -> Pad017
FEATURE [Mesh::Feature] FMT_M_and_T_Guide_8mmx30mm  label="FMT M and T Guide 8mmx30mm"
  Placement = pos=(0,0,0) rot=(0,0,1;3.14159rad)
FEATURE [Sketcher::SketchObject] Sketch036  label="Guide Outline"
  ArcFitTolerance = 1e-06
  ExternalTypes = [0]
  FullyConstrained = true
  MakeInternals = false
  Placement = pos=(0,0,3.1) rot=(0,0,1;0rad)
  _ExternalGeoVersion = 1
  expr: .Placement.Base.z = Spreadsheet.Base_Thickness
  sketch-geometry (148):
    g0: LineSegment StartX=0.784053 StartY=-11.575 StartZ=0 EndX=1.28745 EndY=-11.531 EndZ=0
    g1: LineSegment [constr] StartX=125.65 StartY=-5.7875 StartZ=0 EndX=126.154 EndY=-5.76548 EndZ=0
    g2: LineSegment StartX=1.28745 StartY=-11.531 StartZ=0 EndX=1.785 EndY=-11.3991 EndZ=0
    g3: LineSegment [constr] StartX=126.154 StartY=-5.76548 StartZ=0 EndX=126.655 EndY=-5.69957 EndZ=0
    g4: LineSegment StartX=1.785 StartY=-11.3991 StartZ=0 EndX=2.27298 EndY=-11.1806 EndZ=0
    g5: LineSegment [constr] StartX=126.655 StartY=-5.69957 StartZ=0 EndX=127.148 EndY=-5.5903 EndZ=0
    g6: LineSegment StartX=2.27298 StartY=-11.1806 StartZ=0 EndX=2.74781 EndY=-10.8769 EndZ=0
    g7: LineSegment [constr] StartX=127.148 StartY=-5.5903 StartZ=0 EndX=127.629 EndY=-5.43847 EndZ=0
    g8: LineSegment StartX=2.74781 StartY=-10.8769 StartZ=0 EndX=3.206 EndY=-10.4905 EndZ=0
    g9: LineSegment [constr] StartX=127.629 StartY=-5.43847 StartZ=0 EndX=128.096 EndY=-5.24526 EndZ=0
    g10: LineSegment StartX=3.206 StartY=-10.4905 StartZ=0 EndX=3.64428 EndY=-10.0242 EndZ=0
    g11: LineSegment [constr] StartX=128.096 StartY=-5.24526 StartZ=0 EndX=128.544 EndY=-5.01212 EndZ=0
    g12: LineSegment StartX=3.64428 StartY=-10.0242 StartZ=0 EndX=4.05951 EndY=-9.48168 EndZ=0
    g13: LineSegment [constr] StartX=128.544 StartY=-5.01212 StartZ=0 EndX=128.97 EndY=-4.74084 EndZ=0
    g14: LineSegment StartX=4.05951 StartY=-9.48168 StartZ=0 EndX=4.44878 EndY=-8.86696 EndZ=0
    g15: LineSegment [constr] StartX=128.97 StartY=-4.74084 StartZ=0 EndX=129.37 EndY=-4.43348 EndZ=0
    g16: LineSegment StartX=4.44878 StartY=-8.86696 StartZ=0 EndX=4.80939 EndY=-8.18476 EndZ=0
    g17: LineSegment [constr] StartX=129.37 StartY=-4.43348 StartZ=0 EndX=129.742 EndY=-4.09238 EndZ=0
    g18: LineSegment StartX=4.80939 StartY=-8.18476 StartZ=0 EndX=5.13885 EndY=-7.44027 EndZ=0
    g19: LineSegment [constr] StartX=129.742 StartY=-4.09238 StartZ=0 EndX=130.083 EndY=-3.72013 EndZ=0
    g20: LineSegment StartX=5.13885 StartY=-7.44027 StartZ=0 EndX=5.43493 EndY=-6.63915 EndZ=0
    g21: LineSegment [constr] StartX=130.083 StartY=-3.72013 StartZ=0 EndX=130.391 EndY=-3.31957 EndZ=0
    g22: LineSegment StartX=5.43493 StartY=-6.63915 StartZ=0 EndX=5.69562 EndY=-5.7875 EndZ=0
    g23: LineSegment [constr] StartX=130.391 StartY=-3.31957 StartZ=0 EndX=130.662 EndY=-2.89375 EndZ=0
    g24: LineSegment StartX=5.69562 StartY=-5.7875 StartZ=0 EndX=5.91919 EndY=-4.89181 EndZ=0
    g25: LineSegment [constr] StartX=130.662 StartY=-2.89375 StartZ=0 EndX=130.895 EndY=-2.4459 EndZ=0
    g26: LineSegment StartX=5.91919 StartY=-4.89181 StartZ=0 EndX=6.10414 EndY=-3.95888 EndZ=0
    g27: LineSegment [constr] StartX=130.895 StartY=-2.4459 StartZ=0 EndX=131.088 EndY=-1.97944 EndZ=0
    g28: LineSegment StartX=6.10414 StartY=-3.95888 StartZ=0 EndX=6.24927 EndY=-2.99583 EndZ=0
    g29: LineSegment [constr] StartX=131.088 StartY=-1.97944 StartZ=0 EndX=131.24 EndY=-1.49792 EndZ=0
    g30: LineSegment StartX=6.24927 StartY=-2.99583 StartZ=0 EndX=6.35361 EndY=-2.00998 EndZ=0
    g31: LineSegment [constr] StartX=131.24 StartY=-1.49792 StartZ=0 EndX=131.35 EndY=-1.00499 EndZ=0
    g32: LineSegment StartX=6.35361 StartY=-2.00998 StartZ=0 EndX=6.41649 EndY=-1.00883 EndZ=0
    g33: LineSegment [constr] StartX=131.35 StartY=-1.00499 StartZ=0 EndX=131.415 EndY=-0.504414 EndZ=0
    g34: LineSegment StartX=6.41649 StartY=-1.00883 StartZ=0 EndX=6.4375 EndY=0 EndZ=0
    g35: LineSegment [constr] StartX=131.415 StartY=-0.504414 StartZ=0 EndX=131.438 EndY=0 EndZ=0
    g36: LineSegment StartX=6.4375 StartY=0 StartZ=0 EndX=6.41649 EndY=1.00883 EndZ=0
    g37: LineSegment [constr] StartX=131.438 StartY=0 StartZ=0 EndX=131.415 EndY=0.504414 EndZ=0
    g38: LineSegment StartX=6.41649 StartY=1.00883 StartZ=0 EndX=6.35361 EndY=2.00998 EndZ=0
    g39: LineSegment [constr] StartX=131.415 StartY=0.504414 StartZ=0 EndX=131.35 EndY=1.00499 EndZ=0
    g40: LineSegment StartX=6.35361 StartY=2.00998 StartZ=0 EndX=6.24927 EndY=2.99583 EndZ=0
    g41: LineSegment [constr] StartX=131.35 StartY=1.00499 StartZ=0 EndX=131.24 EndY=1.49792 EndZ=0
    g42: LineSegment StartX=6.24927 StartY=2.99583 StartZ=0 EndX=6.10414 EndY=3.95888 EndZ=0
    g43: LineSegment [constr] StartX=131.24 StartY=1.49792 StartZ=0 EndX=131.088 EndY=1.97944 EndZ=0
    g44: LineSegment StartX=6.10414 StartY=3.95888 StartZ=0 EndX=5.91919 EndY=4.89181 EndZ=0
    g45: LineSegment [constr] StartX=131.088 StartY=1.97944 StartZ=0 EndX=130.895 EndY=2.4459 EndZ=0
    g46: LineSegment StartX=5.91919 StartY=4.89181 StartZ=0 EndX=5.69562 EndY=5.7875 EndZ=0
    g47: LineSegment [constr] StartX=130.895 StartY=2.4459 StartZ=0 EndX=130.662 EndY=2.89375 EndZ=0
    g48: LineSegment StartX=5.69562 StartY=5.7875 StartZ=0 EndX=5.43493 EndY=6.63915 EndZ=0
    g49: LineSegment [constr] StartX=130.662 StartY=2.89375 StartZ=0 EndX=130.391 EndY=3.31957 EndZ=0
    g50: LineSegment StartX=5.43493 StartY=6.63915 StartZ=0 EndX=5.13885 EndY=7.44027 EndZ=0
    g51: LineSegment [constr] StartX=130.391 StartY=3.31957 StartZ=0 EndX=130.083 EndY=3.72013 EndZ=0
    g52: LineSegment StartX=5.13885 StartY=7.44027 StartZ=0 EndX=4.80939 EndY=8.18476 EndZ=0
    g53: LineSegment [constr] StartX=130.083 StartY=3.72013 StartZ=0 EndX=129.742 EndY=4.09238 EndZ=0
    g54: LineSegment StartX=4.80939 StartY=8.18476 StartZ=0 EndX=4.44878 EndY=8.86696 EndZ=0
    g55: LineSegment [constr] StartX=129.742 StartY=4.09238 StartZ=0 EndX=129.37 EndY=4.43348 EndZ=0
    g56: LineSegment StartX=4.44878 StartY=8.86696 StartZ=0 EndX=4.05951 EndY=9.48168 EndZ=0
    g57: LineSegment [constr] StartX=129.37 StartY=4.43348 StartZ=0 EndX=128.97 EndY=4.74084 EndZ=0
    g58: LineSegment StartX=4.05951 StartY=9.48168 StartZ=0 EndX=3.64428 EndY=10.0242 EndZ=0
    g59: LineSegment [constr] StartX=128.97 StartY=4.74084 StartZ=0 EndX=128.544 EndY=5.01212 EndZ=0
    g60: LineSegment StartX=3.64428 StartY=10.0242 StartZ=0 EndX=3.206 EndY=10.4905 EndZ=0
    g61: LineSegment [constr] StartX=128.544 StartY=5.01212 StartZ=0 EndX=128.096 EndY=5.24526 EndZ=0
    g62: LineSegment StartX=3.206 StartY=10.4905 StartZ=0 EndX=2.74781 EndY=10.8769 EndZ=0
    g63: LineSegment [constr] StartX=128.096 StartY=5.24526 StartZ=0 EndX=127.629 EndY=5.43847 EndZ=0
    g64: LineSegment StartX=2.74781 StartY=10.8769 StartZ=0 EndX=2.27298 EndY=11.1806 EndZ=0
    g65: LineSegment [constr] StartX=127.629 StartY=5.43847 StartZ=0 EndX=127.148 EndY=5.5903 EndZ=0
    g66: LineSegment StartX=2.27298 StartY=11.1806 StartZ=0 EndX=1.785 EndY=11.3991 EndZ=0
    g67: LineSegment [constr] StartX=127.148 StartY=5.5903 StartZ=0 EndX=126.655 EndY=5.69957 EndZ=0
    g68: LineSegment StartX=1.785 StartY=11.3991 StartZ=0 EndX=1.28745 EndY=11.531 EndZ=0
    g69: LineSegment [constr] StartX=126.655 StartY=5.69957 StartZ=0 EndX=126.154 EndY=5.76548 EndZ=0
    g70: LineSegment StartX=1.28745 StartY=11.531 StartZ=0 EndX=0.784053 EndY=11.575 EndZ=0
    g71: LineSegment [constr] StartX=126.154 StartY=5.76548 StartZ=0 EndX=125.65 EndY=5.7875 EndZ=0
    g72: LineSegment StartX=0.784053 StartY=11.575 StartZ=0 EndX=-0.515947 EndY=11.575 EndZ=0
    g73: LineSegment [constr] StartX=125.65 StartY=5.7875 StartZ=0 EndX=124.35 EndY=5.7875 EndZ=0
    g74: LineSegment StartX=-0.515947 StartY=11.575 StartZ=0 EndX=-1.02138 EndY=11.531 EndZ=0
    g75: LineSegment [constr] StartX=124.35 StartY=5.7875 StartZ=0 EndX=123.846 EndY=5.76548 EndZ=0
    g76: LineSegment StartX=-1.02138 StartY=11.531 StartZ=0 EndX=-1.52498 EndY=11.3991 EndZ=0
    g77: LineSegment [constr] StartX=123.846 StartY=5.76548 StartZ=0 EndX=123.345 EndY=5.69957 EndZ=0
    g78: LineSegment StartX=-1.52498 StartY=11.3991 StartZ=0 EndX=-2.02285 EndY=11.1806 EndZ=0
    g79: LineSegment [constr] StartX=123.345 StartY=5.69957 StartZ=0 EndX=122.852 EndY=5.5903 EndZ=0
    g80: LineSegment StartX=-2.02285 StartY=11.1806 StartZ=0 EndX=-2.51108 EndY=10.8769 EndZ=0
    g81: LineSegment [constr] StartX=122.852 StartY=5.5903 StartZ=0 EndX=122.371 EndY=5.43847 EndZ=0
    g82: LineSegment StartX=-2.51108 StartY=10.8769 StartZ=0 EndX=-2.9858 EndY=10.4905 EndZ=0
    g83: LineSegment [constr] StartX=122.371 StartY=5.43847 StartZ=0 EndX=121.904 EndY=5.24526 EndZ=0
    g84: LineSegment StartX=-2.9858 StartY=10.4905 StartZ=0 EndX=-3.44322 EndY=10.0242 EndZ=0
    g85: LineSegment [constr] StartX=121.904 StartY=5.24526 StartZ=0 EndX=121.456 EndY=5.01212 EndZ=0
    g86: LineSegment StartX=-3.44322 StartY=10.0242 StartZ=0 EndX=-3.87964 EndY=9.48168 EndZ=0
    g87: LineSegment [constr] StartX=121.456 StartY=5.01212 StartZ=0 EndX=121.03 EndY=4.74084 EndZ=0
    g88: LineSegment StartX=-3.87964 StartY=9.48168 StartZ=0 EndX=-4.29149 EndY=8.86696 EndZ=0
    g89: LineSegment [constr] StartX=121.03 StartY=4.74084 StartZ=0 EndX=120.63 EndY=4.43348 EndZ=0
    g90: LineSegment StartX=-4.29149 StartY=8.86696 StartZ=0 EndX=-4.67537 EndY=8.18476 EndZ=0
    g91: LineSegment [constr] StartX=120.63 StartY=4.43348 StartZ=0 EndX=120.258 EndY=4.09238 EndZ=0
    g92: LineSegment StartX=-4.67537 StartY=8.18476 StartZ=0 EndX=-5.02811 EndY=7.44027 EndZ=0
    g93: LineSegment [constr] StartX=120.258 StartY=4.09238 StartZ=0 EndX=119.917 EndY=3.72013 EndZ=0
    g94: LineSegment StartX=-5.02811 StartY=7.44027 StartZ=0 EndX=-5.34676 EndY=6.63915 EndZ=0
    g95: LineSegment [constr] StartX=119.917 StartY=3.72013 StartZ=0 EndX=119.609 EndY=3.31957 EndZ=0
    g96: LineSegment StartX=-5.34676 StartY=6.63915 StartZ=0 EndX=-5.62862 EndY=5.7875 EndZ=0
    g97: LineSegment [constr] StartX=119.609 StartY=3.31957 StartZ=0 EndX=119.338 EndY=2.89375 EndZ=0
    g98: LineSegment StartX=-5.62862 StartY=5.7875 StartZ=0 EndX=-5.87132 EndY=4.89181 EndZ=0
    g99: LineSegment [constr] StartX=119.338 StartY=2.89375 StartZ=0 EndX=119.105 EndY=2.4459 EndZ=0
    g100: LineSegment StartX=-5.87132 StartY=4.89181 StartZ=0 EndX=-6.0728 EndY=3.95888 EndZ=0
    g101: LineSegment [constr] StartX=119.105 StartY=2.4459 StartZ=0 EndX=118.912 EndY=1.97944 EndZ=0
    g102: LineSegment StartX=-6.0728 StartY=3.95888 StartZ=0 EndX=-6.23132 EndY=2.99583 EndZ=0
    g103: LineSegment [constr] StartX=118.912 StartY=1.97944 StartZ=0 EndX=118.76 EndY=1.49792 EndZ=0
    g104: LineSegment StartX=-6.23132 StartY=2.99583 StartZ=0 EndX=-6.34553 EndY=2.00998 EndZ=0
    g105: LineSegment [constr] StartX=118.76 StartY=1.49792 StartZ=0 EndX=118.65 EndY=1.00499 EndZ=0
    g106: LineSegment StartX=-6.34553 StartY=2.00998 StartZ=0 EndX=-6.41446 EndY=1.00883 EndZ=0
    g107: LineSegment [constr] StartX=118.65 StartY=1.00499 StartZ=0 EndX=118.585 EndY=0.504414 EndZ=0
    g108: LineSegment StartX=-6.41446 StartY=1.00883 StartZ=0 EndX=-6.4375 EndY=0 EndZ=0
    g109: LineSegment [constr] StartX=118.585 StartY=0.504414 StartZ=0 EndX=118.562 EndY=0 EndZ=0
    g110: LineSegment StartX=-6.4375 StartY=0 StartZ=0 EndX=-6.41446 EndY=-1.00883 EndZ=0
    g111: LineSegment [constr] StartX=118.562 StartY=0 StartZ=0 EndX=118.585 EndY=-0.504414 EndZ=0
    g112: LineSegment StartX=-6.41446 StartY=-1.00883 StartZ=0 EndX=-6.34553 EndY=-2.00998 EndZ=0
    g113: LineSegment [constr] StartX=118.585 StartY=-0.504414 StartZ=0 EndX=118.65 EndY=-1.00499 EndZ=0
    g114: LineSegment StartX=-6.34553 StartY=-2.00998 StartZ=0 EndX=-6.23132 EndY=-2.99583 EndZ=0
    g115: LineSegment [constr] StartX=118.65 StartY=-1.00499 StartZ=0 EndX=118.76 EndY=-1.49792 EndZ=0
    g116: LineSegment StartX=-6.23132 StartY=-2.99583 StartZ=0 EndX=-6.0728 EndY=-3.95888 EndZ=0
    g117: LineSegment [constr] StartX=118.76 StartY=-1.49792 StartZ=0 EndX=118.912 EndY=-1.97944 EndZ=0
    g118: LineSegment StartX=-6.0728 StartY=-3.95888 StartZ=0 EndX=-5.87132 EndY=-4.89181 EndZ=0
    g119: LineSegment [constr] StartX=118.912 StartY=-1.97944 StartZ=0 EndX=119.105 EndY=-2.4459 EndZ=0
    g120: LineSegment StartX=-5.87132 StartY=-4.89181 StartZ=0 EndX=-5.62862 EndY=-5.7875 EndZ=0
    g121: LineSegment [constr] StartX=119.105 StartY=-2.4459 StartZ=0 EndX=119.338 EndY=-2.89375 EndZ=0
    g122: LineSegment StartX=-5.62862 StartY=-5.7875 StartZ=0 EndX=-5.34676 EndY=-6.63915 EndZ=0
    g123: LineSegment [constr] StartX=119.338 StartY=-2.89375 StartZ=0 EndX=119.609 EndY=-3.31957 EndZ=0
    g124: LineSegment StartX=-5.34676 StartY=-6.63915 StartZ=0 EndX=-5.02811 EndY=-7.44027 EndZ=0
    g125: LineSegment [constr] StartX=119.609 StartY=-3.31957 StartZ=0 EndX=119.917 EndY=-3.72013 EndZ=0
    g126: LineSegment StartX=-5.02811 StartY=-7.44027 StartZ=0 EndX=-4.67537 EndY=-8.18476 EndZ=0
    g127: LineSegment [constr] StartX=119.917 StartY=-3.72013 StartZ=0 EndX=120.258 EndY=-4.09238 EndZ=0
    g128: LineSegment StartX=-4.67537 StartY=-8.18476 StartZ=0 EndX=-4.29149 EndY=-8.86696 EndZ=0
    g129: LineSegment [constr] StartX=120.258 StartY=-4.09238 StartZ=0 EndX=120.63 EndY=-4.43348 EndZ=0
    g130: LineSegment StartX=-4.29149 StartY=-8.86696 StartZ=0 EndX=-3.87964 EndY=-9.48168 EndZ=0
    g131: LineSegment [constr] StartX=120.63 StartY=-4.43348 StartZ=0 EndX=121.03 EndY=-4.74084 EndZ=0
    g132: LineSegment StartX=-3.87964 StartY=-9.48168 StartZ=0 EndX=-3.44322 EndY=-10.0242 EndZ=0
    g133: LineSegment [constr] StartX=121.03 StartY=-4.74084 StartZ=0 EndX=121.456 EndY=-5.01212 EndZ=0
    g134: LineSegment StartX=-3.44322 StartY=-10.0242 StartZ=0 EndX=-2.9858 EndY=-10.4905 EndZ=0
    g135: LineSegment [constr] StartX=121.456 StartY=-5.01212 StartZ=0 EndX=121.904 EndY=-5.24526 EndZ=0
    g136: LineSegment StartX=-2.9858 StartY=-10.4905 StartZ=0 EndX=-2.51108 EndY=-10.8769 EndZ=0
    g137: LineSegment [constr] StartX=121.904 StartY=-5.24526 StartZ=0 EndX=122.371 EndY=-5.43847 EndZ=0
    g138: LineSegment StartX=-2.51108 StartY=-10.8769 StartZ=0 EndX=-2.02285 EndY=-11.1806 EndZ=0
    g139: LineSegment [constr] StartX=122.371 StartY=-5.43847 StartZ=0 EndX=122.852 EndY=-5.5903 EndZ=0
    g140: LineSegment StartX=-2.02285 StartY=-11.1806 StartZ=0 EndX=-1.52498 EndY=-11.3991 EndZ=0
    g141: LineSegment [constr] StartX=122.852 StartY=-5.5903 StartZ=0 EndX=123.345 EndY=-5.69957 EndZ=0
    g142: LineSegment StartX=-1.52498 StartY=-11.3991 StartZ=0 EndX=-1.02138 EndY=-11.531 EndZ=0
    g143: LineSegment [constr] StartX=123.345 StartY=-5.69957 StartZ=0 EndX=123.846 EndY=-5.76548 EndZ=0
    g144: LineSegment StartX=-1.02138 StartY=-11.531 StartZ=0 EndX=-0.515947 EndY=-11.575 EndZ=0
    g145: LineSegment [constr] StartX=123.846 StartY=-5.76548 StartZ=0 EndX=124.35 EndY=-5.7875 EndZ=0
    g146: LineSegment StartX=-0.515947 StartY=-11.575 StartZ=0 EndX=0.784053 EndY=-11.575 EndZ=0
    g147: LineSegment [constr] StartX=124.35 StartY=-5.7875 StartZ=0 EndX=125.65 EndY=-5.7875 EndZ=0
  constraints (297):
    c: Block(g0)
    c: Block(g1)
    c: Block(g2)
    c: Coincident(g0,g2)
    c: Block(g3)
    c: Coincident(g1,g3)
    c: Block(g4)
    c: Coincident(g2,g4)
    c: Block(g5)
    c: Coincident(g3,g5)
    c: Block(g6)
    c: Coincident(g4,g6)
    c: Block(g7)
    c: Coincident(g5,g7)
    c: Block(g8)
    c: Coincident(g6,g8)
    c: Block(g9)
    c: Coincident(g7,g9)
    c: Block(g10)
    c: Coincident(g8,g10)
    c: Block(g11)
    c: Coincident(g9,g11)
    c: Block(g12)
    c: Coincident(g10,g12)
    c: Block(g13)
    c: Coincident(g11,g13)
    c: Block(g14)
    c: Coincident(g12,g14)
    c: Block(g15)
    c: Coincident(g13,g15)
    c: Block(g16)
    c: Coincident(g14,g16)
    c: Block(g17)
    c: Coincident(g15,g17)
    c: Block(g18)
    c: Coincident(g16,g18)
    c: Block(g19)
    c: Coincident(g17,g19)
    c: Block(g20)
    c: Coincident(g18,g20)
    c: Block(g21)
    c: Coincident(g19,g21)
    c: Block(g22)
    c: Coincident(g20,g22)
    c: Block(g23)
    c: Coincident(g21,g23)
    c: Block(g24)
    c: Coincident(g22,g24)
    c: Block(g25)
    c: Coincident(g23,g25)
    c: Block(g26)
    c: Coincident(g24,g26)
    c: Block(g27)
    c: Coincident(g25,g27)
    c: Block(g28)
    c: Coincident(g26,g28)
    c: Block(g29)
    c: Coincident(g27,g29)
    c: Block(g30)
    c: Coincident(g28,g30)
    c: Block(g31)
    c: Coincident(g29,g31)
    c: Block(g32)
    c: Coincident(g30,g32)
    c: Block(g33)
    c: Coincident(g31,g33)
    c: Block(g34)
    c: Coincident(g32,g34)
    c: Block(g35)
    c: Coincident(g33,g35)
    c: Block(g36)
    c: Coincident(g34,g36)
    c: Block(g37)
    c: Coincident(g35,g37)
    c: Block(g38)
    c: Coincident(g36,g38)
    c: Block(g39)
    c: Coincident(g37,g39)
    c: Block(g40)
    c: Coincident(g38,g40)
    c: Block(g41)
    c: Coincident(g39,g41)
    c: Block(g42)
    c: Coincident(g40,g42)
    c: Block(g43)
    c: Coincident(g41,g43)
    c: Block(g44)
    c: Coincident(g42,g44)
    c: Block(g45)
    c: Coincident(g43,g45)
    c: Block(g46)
    c: Coincident(g44,g46)
    c: Block(g47)
    c: Coincident(g45,g47)
    c: Block(g48)
    c: Coincident(g46,g48)
    c: Block(g49)
    c: Coincident(g47,g49)
    c: Block(g50)
    c: Coincident(g48,g50)
    c: Block(g51)
    c: Coincident(g49,g51)
    c: Block(g52)
    c: Coincident(g50,g52)
    c: Block(g53)
    c: Coincident(g51,g53)
    c: Block(g54)
    c: Coincident(g52,g54)
    c: Block(g55)
    c: Coincident(g53,g55)
    c: Block(g56)
    c: Coincident(g54,g56)
    c: Block(g57)
    c: Coincident(g55,g57)
    c: Block(g58)
    c: Coincident(g56,g58)
    c: Block(g59)
    c: Coincident(g57,g59)
    c: Block(g60)
    c: Coincident(g58,g60)
    c: Block(g61)
    c: Coincident(g59,g61)
    c: Block(g62)
    c: Coincident(g60,g62)
    c: Block(g63)
    c: Coincident(g61,g63)
    c: Block(g64)
    c: Coincident(g62,g64)
    c: Block(g65)
    c: Coincident(g63,g65)
    c: Block(g66)
    c: Coincident(g64,g66)
    c: Block(g67)
    c: Coincident(g65,g67)
    c: Block(g68)
    c: Coincident(g66,g68)
    c: Block(g69)
    c: Coincident(g67,g69)
    c: Block(g70)
    c: Coincident(g68,g70)
    c: Block(g71)
    c: Coincident(g69,g71)
    c: Block(g72)
    c: Coincident(g70,g72)
    c: Block(g73)
    c: Coincident(g71,g73)
    c: Block(g74)
    c: Coincident(g72,g74)
    c: Block(g75)
    c: Coincident(g73,g75)
    c: Block(g76)
    c: Coincident(g74,g76)
    c: Block(g77)
    c: Coincident(g75,g77)
    c: Block(g78)
    c: Coincident(g76,g78)
    c: Block(g79)
    c: Coincident(g77,g79)
    c: Block(g80)
    c: Coincident(g78,g80)
    c: Block(g81)
    c: Coincident(g79,g81)
    c: Block(g82)
    c: Coincident(g80,g82)
    c: Block(g83)
    c: Coincident(g81,g83)
    c: Block(g84)
    c: Coincident(g82,g84)
    c: Block(g85)
    c: Coincident(g83,g85)
    c: Block(g86)
    c: Coincident(g84,g86)
    c: Block(g87)
    c: Coincident(g85,g87)
    c: Block(g88)
    c: Coincident(g86,g88)
    c: Block(g89)
    c: Coincident(g87,g89)
    c: Block(g90)
    c: Coincident(g88,g90)
    c: Block(g91)
    c: Coincident(g89,g91)
    c: Block(g92)
    c: Coincident(g90,g92)
    c: Block(g93)
    c: Coincident(g91,g93)
    c: Block(g94)
    c: Coincident(g92,g94)
    c: Block(g95)
    c: Coincident(g93,g95)
    c: Block(g96)
    c: Coincident(g94,g96)
    c: Block(g97)
    c: Coincident(g95,g97)
    c: Block(g98)
    c: Coincident(g96,g98)
    c: Block(g99)
    c: Coincident(g97,g99)
    c: Block(g100)
    c: Coincident(g98,g100)
    c: Block(g101)
    c: Coincident(g99,g101)
    c: Block(g102)
    c: Coincident(g100,g102)
    c: Block(g103)
    c: Coincident(g101,g103)
    c: Block(g104)
    c: Coincident(g102,g104)
    c: Block(g105)
    c: Coincident(g103,g105)
    c: Block(g106)
    c: Coincident(g104,g106)
    c: Block(g107)
    c: Coincident(g105,g107)
    c: Block(g108)
    c: Coincident(g106,g108)
    c: Block(g109)
    c: Coincident(g107,g109)
    c: Block(g110)
    c: Coincident(g108,g110)
    c: Block(g111)
    c: Coincident(g109,g111)
    c: Block(g112)
    c: Coincident(g110,g112)
    c: Block(g113)
    c: Coincident(g111,g113)
    c: Block(g114)
    c: Coincident(g112,g114)
    c: Block(g115)
    c: Coincident(g113,g115)
    c: Block(g116)
    c: Coincident(g114,g116)
    c: Block(g117)
    c: Coincident(g115,g117)
    c: Block(g118)
    c: Coincident(g116,g118)
    c: Block(g119)
    c: Coincident(g117,g119)
    c: Block(g120)
    c: Coincident(g118,g120)
    c: Block(g121)
    c: Coincident(g119,g121)
    c: Block(g122)
    c: Coincident(g120,g122)
    c: Block(g123)
    c: Coincident(g121,g123)
    c: Block(g124)
    c: Coincident(g122,g124)
    c: Block(g125)
    c: Coincident(g123,g125)
    c: Block(g126)
    c: Coincident(g124,g126)
    c: Block(g127)
    c: Coincident(g125,g127)
    c: Block(g128)
    c: Coincident(g126,g128)
    c: Block(g129)
    c: Coincident(g127,g129)
    c: Block(g130)
    c: Coincident(g128,g130)
    c: Block(g131)
    c: Coincident(g129,g131)
    c: Block(g132)
    c: Coincident(g130,g132)
    c: Block(g133)
    c: Coincident(g131,g133)
    c: Block(g134)
    c: Coincident(g132,g134)
    c: Block(g135)
    c: Coincident(g133,g135)
    c: Block(g136)
    c: Coincident(g134,g136)
    c: Block(g137)
    c: Coincident(g135,g137)
    c: Block(g138)
    c: Coincident(g136,g138)
    c: Block(g139)
    c: Coincident(g137,g139)
    c: Block(g140)
    c: Coincident(g138,g140)
    c: Block(g141)
    c: Coincident(g139,g141)
    c: Block(g142)
    c: Coincident(g140,g142)
    c: Block(g143)
    c: Coincident(g141,g143)
    c: Block(g144)
    c: Coincident(g142,g144)
    c: Block(g145)
    c: Coincident(g143,g145)
    c: Block(g146)
    c: Coincident(g144,g146)
    c: Coincident(g146,g0)
    c: Block(g147)
    c: Coincident(g145,g147)
    c: Coincident(g147,g1)
    c: Distance(g72,g72) = 1.3
FEATURE [App::Point] Origin023  label="Origin030"
  Role = Origin
FEATURE [PartDesign::Pad] Pad018
  Direction = (0,0,1)
  Length = 6.6
  Length2 = 10
  Placement = pos=(0,0,3.1) rot=(0,0,1;0rad)
  Profile = -> Sketch036
  ReferenceAxis = -> Sketch036 [N_Axis]
  SideType = 0
  Suppressed = false
  TaperAngle = -9.22
  Type = 0
  Type2 = 0
  expr: Length = Spreadsheet.Upper_Plane - Spreadsheet.Base_Thickness
  expr: TaperAngle = -Spreadsheet.Pin_Angle
FEATURE [Sketcher::SketchObject] Sketch037
  ArcFitTolerance = 1e-06
  AttachmentSupport = -> [DatumPlane002]
  ExternalTypes = [0]
  FullyConstrained = false
  MakeInternals = false
  MapMode = 5
  Placement = pos=(0,0,3.1) rot=(0,0,1;0rad)
  _ExternalGeoVersion = 1
  sketch-geometry (6):
    g0: LineSegment StartX=-0.5 StartY=14.4396 StartZ=0 EndX=-0.5 EndY=-14.4396 EndZ=0
    g1: LineSegment StartX=-0.5 StartY=-14.4396 StartZ=0 EndX=0.5 EndY=-14.4396 EndZ=0
    g2: LineSegment StartX=0.5 StartY=-14.4396 StartZ=0 EndX=0.5 EndY=14.4396 EndZ=0
    g3: LineSegment StartX=0.5 StartY=14.4396 StartZ=0 EndX=-0.5 EndY=14.4396 EndZ=0
    g4: GeomPoint [constr] X=0 Y=1e-16 Z=0
    g5: Circle CenterX=4.63741 CenterY=3.99915 CenterZ=0 NormalX=0 NormalY=0 NormalZ=1 AngleXU=0 Radius=0.5
  constraints (12):
    c: Coincident(g0,g1)
    c: Coincident(g1,g2)
    c: Coincident(g2,g3)
    c: Coincident(g3,g0)
    c: Vertical(g0)
    c: Horizontal(g1)
    c: Horizontal(g3)
    c: Symmetric(g2,g0,g4)
    c: PointOnObject(g4,g-2)
    c: Distance(g3,g3) = 1
    c: Symmetric(g1,g2,g-1)
    c: Diameter(g5) = 1
FEATURE [PartDesign::Body] Body011  label="Guide"
  AllowCompound = false
  Group = -> [Sketch036,Pad018,Sketch037]
  Origin = -> Origin022
  Tip = -> Pad018
FEATURE [Part::Cut] Cut003  label="Guide with Slot"
  Base = -> Body011
  Tool = -> Loft
FEATURE [Part::Fuse] Fusion009  label="M & T Guide"
  Base = -> Fusion007
  Tool = -> Cut003
FEATURE [Part::Fuse] Fusion011  label="Y Tenon"
  Base = -> Fusion007
  Tool = -> Body005
FEATURE [Mesh::Feature] FMT_M_and_T_Guide_6mmx35mm  label="FMT M and T Guide 6mmx35mm"
  Placement = pos=(0,0,0) rot=(0,0,1;3.14159rad)
note: 4 file-system paths scrubbed to <path> (originals preserved in the JSON sidecar)
